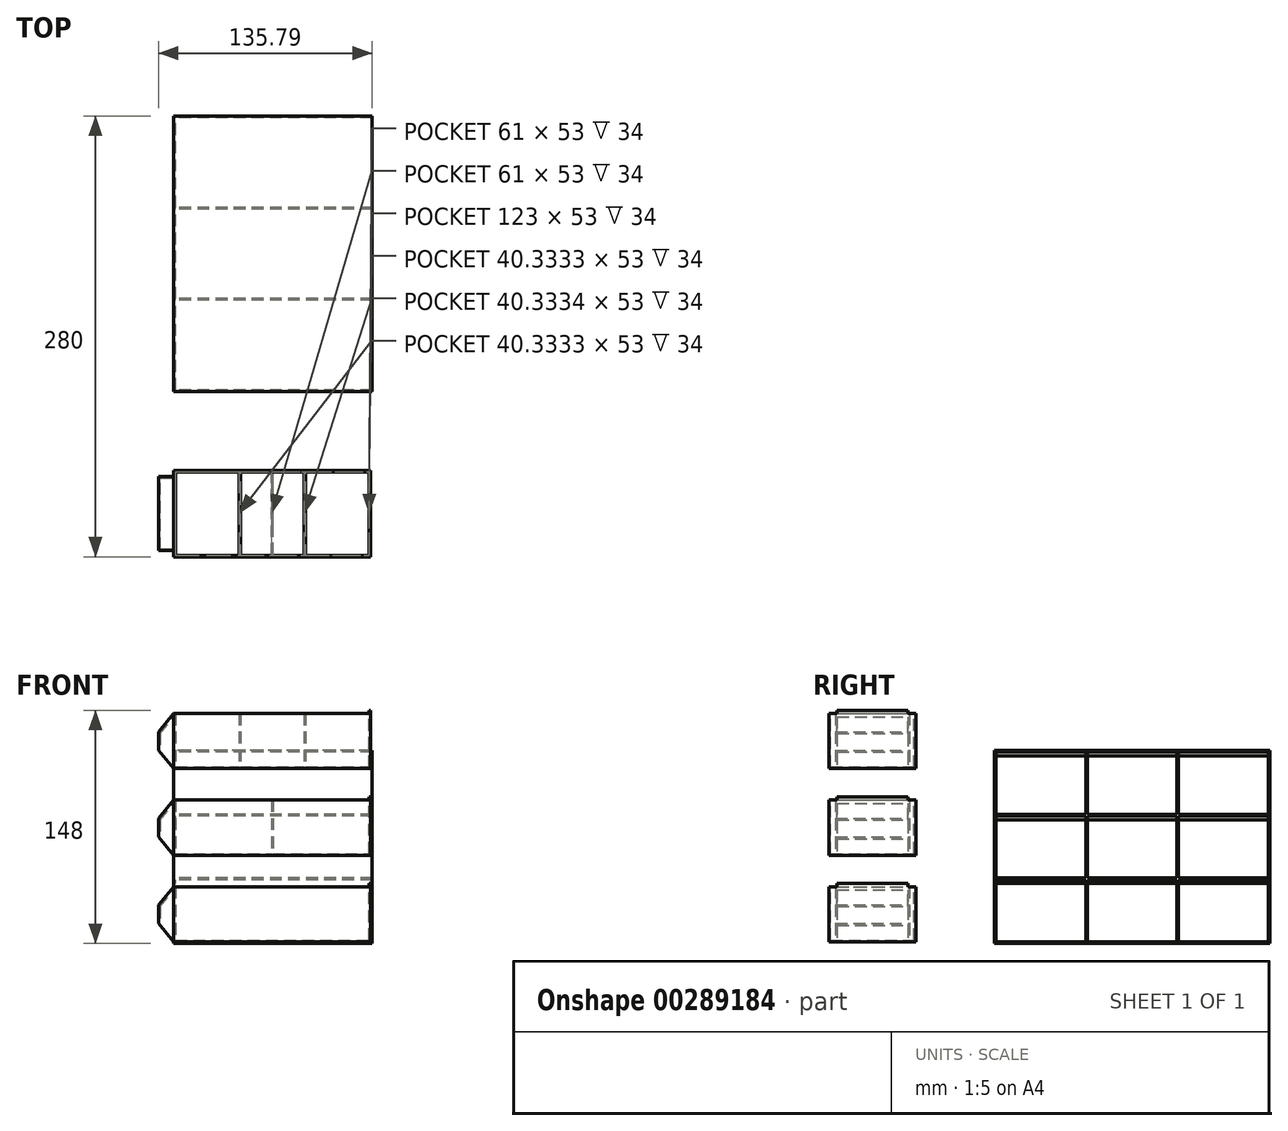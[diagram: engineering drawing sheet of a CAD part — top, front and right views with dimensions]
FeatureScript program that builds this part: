
annotation { "Feature Type Name" : "Feature", "Feature Type Description" : "" }
export const myFeature = defineFeature(function(context is Context, id is Id, definition is map)
    precondition{}
    {
        {
            assignVariable(context, id + "F0", {"name" : "DrawerDepth", "anyValue" : 125});
        }
        {
            assignVariable(context, id + "F1", {"name" : "DrawerWidth", "anyValue" : 55});
        }
        {
            assignVariable(context, id + "F2", {"name" : "Thickness", "anyValue" : 1});
        }
        {
            var Q0;
            Q0=qCreatedBy(makeId("Front.planeOp"),FACE);
            var sketch = newSketch(context, id + "F3", { "sketchPlane" : qUnion([Q0])});
            skLineSegment(sketch, "E0", {"start": v(0, 11.67) * mm, "end": v(0, 0) * mm});
            skLineSegment(sketch, "E1", {"start": v(0, 0) * mm, "end": v(125, 0) * mm});
            skLineSegment(sketch, "E2", {"start": v(125, 37) * mm, "end": v(124, 37) * mm});
            skLineSegment(sketch, "E3", {"start": v(124, 37) * mm, "end": v(124, 35) * mm});
            skLineSegment(sketch, "E4", {"start": v(0, 35) * mm, "end": v(-9.79, 23.33) * mm});
            skLineSegment(sketch, "E5", {"start": v(-9.79, 23.33) * mm, "end": v(-9.79, 11.67) * mm});
            skLineSegment(sketch, "E6", {"start": v(-9.79, 11.67) * mm, "end": v(0, 0) * mm});
            skLineSegment(sketch, "E7", {"start": v(0, 35) * mm, "end": v(0, 23.33) * mm});
            skLineSegment(sketch, "E8", {"start": v(0, 23.33) * mm, "end": v(0, 11.67) * mm});
            skLineSegment(sketch, "E9", {"start": v(0, 35) * mm, "end": v(1, 35) * mm});
            skLineSegment(sketch, "E10", {"start": v(1, 35) * mm, "end": v(124, 35) * mm});
            skLineSegment(sketch, "E11", {"start": v(125, 37) * mm, "end": v(125, 1) * mm});
            skLineSegment(sketch, "E12", {"start": v(125, 1) * mm, "end": v(125, 0) * mm});
            skLineSegment(sketch, "E13", {"start": v(1, 35) * mm, "end": v(1, 1) * mm});
            skLineSegment(sketch, "E14", {"start": v(1, 1) * mm, "end": v(124, 1) * mm});
            skLineSegment(sketch, "E15", {"start": v(124, 1) * mm, "end": v(124, 35) * mm});
            skLineSegment(sketch, "E16", {"start": v(124, 35) * mm, "end": v(125, 35) * mm});
            skLineSegment(sketch, "E17", {"start": v(-8.79, 22.5) * mm, "end": v(-8.79, 10.47) * mm});
            skLineSegment(sketch, "E18", {"start": v(-8.79, 22.5) * mm, "end": v(0, 32.97) * mm});
            skLineSegment(sketch, "E19", {"start": v(-9.79, 23.33) * mm, "end": v(-8.79, 22.5) * mm, "construction": true});
            skLineSegment(sketch, "E20", {"start": v(0, 66.67) * mm, "end": v(0, 55) * mm});
            skLineSegment(sketch, "E21", {"start": v(0, 55) * mm, "end": v(125, 55) * mm});
            skLineSegment(sketch, "E22", {"start": v(125, 92) * mm, "end": v(124, 92) * mm});
            skLineSegment(sketch, "E23", {"start": v(124, 92) * mm, "end": v(124, 90) * mm});
            skLineSegment(sketch, "E24", {"start": v(0, 90) * mm, "end": v(-9.79, 78.33) * mm});
            skLineSegment(sketch, "E25", {"start": v(-9.79, 78.33) * mm, "end": v(-9.79, 66.67) * mm});
            skLineSegment(sketch, "E26", {"start": v(-9.79, 66.67) * mm, "end": v(0, 55) * mm});
            skLineSegment(sketch, "E27", {"start": v(0, 90) * mm, "end": v(0, 78.33) * mm});
            skLineSegment(sketch, "E28", {"start": v(0, 78.33) * mm, "end": v(0, 66.67) * mm});
            skLineSegment(sketch, "E29", {"start": v(0, 90) * mm, "end": v(1, 90) * mm});
            skLineSegment(sketch, "E30", {"start": v(125, 92) * mm, "end": v(125, 56) * mm});
            skLineSegment(sketch, "E31", {"start": v(125, 56) * mm, "end": v(125, 55) * mm});
            skLineSegment(sketch, "E32", {"start": v(1, 90) * mm, "end": v(1, 56) * mm});
            skLineSegment(sketch, "E33", {"start": v(1, 56) * mm, "end": v(124, 56) * mm});
            skLineSegment(sketch, "E34", {"start": v(124, 56) * mm, "end": v(124, 90) * mm});
            skLineSegment(sketch, "E35", {"start": v(124, 90) * mm, "end": v(125, 90) * mm});
            skLineSegment(sketch, "E36", {"start": v(-8.79, 77.5) * mm, "end": v(-8.79, 65.47) * mm});
            skLineSegment(sketch, "E37", {"start": v(-8.79, 77.5) * mm, "end": v(0, 87.97) * mm});
            skLineSegment(sketch, "E38", {"start": v(-9.79, 78.33) * mm, "end": v(-8.79, 77.5) * mm, "construction": true});
            skLineSegment(sketch, "E39", {"start": v(1, 90) * mm, "end": v(62, 90) * mm});
            skLineSegment(sketch, "E40", {"start": v(62, 90) * mm, "end": v(63, 90) * mm});
            skLineSegment(sketch, "E41", {"start": v(63, 90) * mm, "end": v(124, 90) * mm});
            skLineSegment(sketch, "E42", {"start": v(62, 90) * mm, "end": v(62, 56) * mm});
            skLineSegment(sketch, "E43", {"start": v(63, 90) * mm, "end": v(63, 56) * mm});
            skLineSegment(sketch, "E44", {"start": v(0, 121.67) * mm, "end": v(0, 110) * mm});
            skLineSegment(sketch, "E45", {"start": v(0, 110) * mm, "end": v(125, 110) * mm});
            skLineSegment(sketch, "E46", {"start": v(125, 147) * mm, "end": v(124, 147) * mm});
            skLineSegment(sketch, "E47", {"start": v(124, 147) * mm, "end": v(124, 145) * mm});
            skLineSegment(sketch, "E48", {"start": v(0, 145) * mm, "end": v(-9.79, 133.33) * mm});
            skLineSegment(sketch, "E49", {"start": v(-9.79, 133.33) * mm, "end": v(-9.79, 121.67) * mm});
            skLineSegment(sketch, "E50", {"start": v(-9.79, 121.67) * mm, "end": v(0, 110) * mm});
            skLineSegment(sketch, "E51", {"start": v(0, 145) * mm, "end": v(0, 133.33) * mm});
            skLineSegment(sketch, "E52", {"start": v(0, 133.33) * mm, "end": v(0, 121.67) * mm});
            skLineSegment(sketch, "E53", {"start": v(0, 145) * mm, "end": v(1, 145) * mm});
            skLineSegment(sketch, "E54", {"start": v(125, 147) * mm, "end": v(125, 111) * mm});
            skLineSegment(sketch, "E55", {"start": v(125, 111) * mm, "end": v(125, 110) * mm});
            skLineSegment(sketch, "E56", {"start": v(1, 145) * mm, "end": v(1, 111) * mm});
            skLineSegment(sketch, "E57", {"start": v(1, 111) * mm, "end": v(124, 111) * mm});
            skLineSegment(sketch, "E58", {"start": v(124, 111) * mm, "end": v(124, 145) * mm});
            skLineSegment(sketch, "E59", {"start": v(124, 145) * mm, "end": v(125, 145) * mm});
            skLineSegment(sketch, "E60", {"start": v(-8.79, 132.5) * mm, "end": v(-8.79, 120.47) * mm});
            skLineSegment(sketch, "E61", {"start": v(-8.79, 132.5) * mm, "end": v(0, 142.97) * mm});
            skLineSegment(sketch, "E62", {"start": v(-9.79, 133.33) * mm, "end": v(-8.79, 132.5) * mm, "construction": true});
            skLineSegment(sketch, "E63", {"start": v(1, 145) * mm, "end": v(41.33, 145) * mm});
            skLineSegment(sketch, "E64", {"start": v(41.33, 145) * mm, "end": v(42.33, 145) * mm});
            skLineSegment(sketch, "E65", {"start": v(42.33, 145) * mm, "end": v(82.67, 145) * mm});
            skLineSegment(sketch, "E66", {"start": v(82.67, 145) * mm, "end": v(83.67, 145) * mm});
            skLineSegment(sketch, "E67", {"start": v(83.67, 145) * mm, "end": v(124, 145) * mm});
            skLineSegment(sketch, "E68", {"start": v(41.33, 145) * mm, "end": v(41.33, 111) * mm});
            skLineSegment(sketch, "E69", {"start": v(42.33, 145) * mm, "end": v(42.33, 111) * mm});
            skLineSegment(sketch, "E70", {"start": v(82.67, 145) * mm, "end": v(82.67, 111) * mm});
            skLineSegment(sketch, "E71", {"start": v(83.67, 145) * mm, "end": v(83.67, 111) * mm});
            skSolve(sketch);
        }
        {
            var Q0;
            Q0=makeQuery(id+"F3.imprint","IMPRINT",FACE,{"disambiguationData":[TD([[makeQuery(id+"F3.imprint","IMPRINT",EDGE,{"derivedFrom":sQuery(id+"F3.wireOp",EDGE,"E0")}),1.0]])]});
            var Q1;
            Q1=makeQuery(id+"F3.imprint","IMPRINT",FACE,{"disambiguationData":[TD([[makeQuery(id+"F3.imprint","IMPRINT",EDGE,{"derivedFrom":sQuery(id+"F3.wireOp",EDGE,"E20")}),1.0]])]});
            var Q2;
            Q2=makeQuery(id+"F3.imprint","IMPRINT",FACE,{"disambiguationData":[TD([[makeQuery(id+"F3.imprint","IMPRINT",EDGE,{"derivedFrom":sQuery(id+"F3.wireOp",EDGE,"E44")}),1.0]])]});
            var Q3;
            Q3=makeQuery(id+"F3.imprint","IMPRINT",FACE,{"disambiguationData":[TD([[makeQuery(id+"F3.imprint","IMPRINT",EDGE,{"derivedFrom":sQuery(id+"F3.wireOp",EDGE,"E40")}),-1.0]])]});
            var Q4;
            Q4=makeQuery(id+"F3.imprint","IMPRINT",FACE,{"disambiguationData":[TD([[makeQuery(id+"F3.imprint","IMPRINT",EDGE,{"derivedFrom":sQuery(id+"F3.wireOp",EDGE,"E64")}),-1.0]])]});
            var Q5;
            Q5=makeQuery(id+"F3.imprint","IMPRINT",FACE,{"disambiguationData":[TD([[makeQuery(id+"F3.imprint","IMPRINT",EDGE,{"derivedFrom":sQuery(id+"F3.wireOp",EDGE,"E66")}),-1.0]])]});
            extrude(context, id + "F4", {"entities" : qUnion([Q0, Q1, Q2, Q3, Q4, Q5]), "depth" : (getVariable(context, 'DrawerWidth')) * mm});
        }
        {
            var Q0;
            Q0=makeQuery(id+"F3.imprint","IMPRINT",FACE,{"disambiguationData":[TD([[makeQuery(id+"F3.imprint","IMPRINT",EDGE,{"derivedFrom":sQuery(id+"F3.wireOp",EDGE,"E10")}),-1.0]])]});
            var Q1;
            {var subQ0=sQuery(id+"F3.wireOp",EDGE,"E56");Q1=makeQuery(id+"F3.imprint","IMPRINT",FACE,{"disambiguationData":[TD([[makeQuery(id+"F3.imprint","IMPRINT",EDGE,{"derivedFrom":subQ0}),1.0]])]});}
            var Q2;
            Q2=makeQuery(id+"F3.imprint","IMPRINT",FACE,{"disambiguationData":[TD([[makeQuery(id+"F3.imprint","IMPRINT",EDGE,{"derivedFrom":sQuery(id+"F3.wireOp",EDGE,"E65")}),-1.0]])]});
            var Q3;
            {var subQ0=sQuery(id+"F3.wireOp",EDGE,"E58");Q3=makeQuery(id+"F3.imprint","IMPRINT",FACE,{"disambiguationData":[TD([[makeQuery(id+"F3.imprint","IMPRINT",EDGE,{"derivedFrom":subQ0}),1.0]])]});}
            var Q4;
            {var subQ0=sQuery(id+"F3.wireOp",EDGE,"E34");Q4=makeQuery(id+"F3.imprint","IMPRINT",FACE,{"disambiguationData":[TD([[makeQuery(id+"F3.imprint","IMPRINT",EDGE,{"derivedFrom":subQ0}),1.0]])]});}
            var Q5;
            {var subQ0=sQuery(id+"F3.wireOp",EDGE,"E32");Q5=makeQuery(id+"F3.imprint","IMPRINT",FACE,{"disambiguationData":[TD([[makeQuery(id+"F3.imprint","IMPRINT",EDGE,{"derivedFrom":subQ0}),1.0]])]});}
            extrude(context, id + "F5", {"entities" : qUnion([Q0, Q1, Q2, Q3, Q4, Q5]), "operationType" : NewBodyOperationType.ADD, "depth" : (getVariable(context, 'Thickness')) * mm});
        }
        {
            var Q0;
            Q0=makeQuery(id+"F3.imprint","IMPRINT",FACE,{"disambiguationData":[TD([[makeQuery(id+"F3.imprint","IMPRINT",EDGE,{"derivedFrom":sQuery(id+"F3.wireOp",EDGE,"E10")}),-1.0]])]});
            var Q1;
            {var subQ0=sQuery(id+"F3.wireOp",EDGE,"E32");Q1=makeQuery(id+"F3.imprint","IMPRINT",FACE,{"disambiguationData":[TD([[makeQuery(id+"F3.imprint","IMPRINT",EDGE,{"derivedFrom":subQ0}),1.0]])]});}
            var Q2;
            {var subQ0=sQuery(id+"F3.wireOp",EDGE,"E34");Q2=makeQuery(id+"F3.imprint","IMPRINT",FACE,{"disambiguationData":[TD([[makeQuery(id+"F3.imprint","IMPRINT",EDGE,{"derivedFrom":subQ0}),1.0]])]});}
            var Q3;
            {var subQ0=sQuery(id+"F3.wireOp",EDGE,"E56");Q3=makeQuery(id+"F3.imprint","IMPRINT",FACE,{"disambiguationData":[TD([[makeQuery(id+"F3.imprint","IMPRINT",EDGE,{"derivedFrom":subQ0}),1.0]])]});}
            var Q4;
            Q4=makeQuery(id+"F3.imprint","IMPRINT",FACE,{"disambiguationData":[TD([[makeQuery(id+"F3.imprint","IMPRINT",EDGE,{"derivedFrom":sQuery(id+"F3.wireOp",EDGE,"E65")}),-1.0]])]});
            var Q5;
            {var subQ0=sQuery(id+"F3.wireOp",EDGE,"E58");Q5=makeQuery(id+"F3.imprint","IMPRINT",FACE,{"disambiguationData":[TD([[makeQuery(id+"F3.imprint","IMPRINT",EDGE,{"derivedFrom":subQ0}),1.0]])]});}
            extrude(context, id + "F6", {"entities" : qUnion([Q0, Q1, Q2, Q3, Q4, Q5]), "operationType" : NewBodyOperationType.ADD, "depth" : (getVariable(context, 'DrawerWidth')) * mm, "hasSecondDirection" : true, "secondDirectionOppositeDirection" : false, "secondDirectionDepth" : (getVariable(context, 'DrawerWidth') - getVariable(context, 'Thickness')) * mm});
        }
        {
            var Q0;
            {var subQ0=sQuery(id+"F3.wireOp",EDGE,"E2");Q0=makeQuery(id+"F3.imprint","IMPRINT",FACE,{"disambiguationData":[TD([[makeQuery(id+"F3.imprint","IMPRINT",EDGE,{"derivedFrom":subQ0}),1.0]])]});}
            var Q1;
            {var subQ0=sQuery(id+"F3.wireOp",EDGE,"E22");Q1=makeQuery(id+"F3.imprint","IMPRINT",FACE,{"disambiguationData":[TD([[makeQuery(id+"F3.imprint","IMPRINT",EDGE,{"derivedFrom":subQ0}),1.0]])]});}
            var Q2;
            {var subQ0=sQuery(id+"F3.wireOp",EDGE,"E46");Q2=makeQuery(id+"F3.imprint","IMPRINT",FACE,{"disambiguationData":[TD([[makeQuery(id+"F3.imprint","IMPRINT",EDGE,{"derivedFrom":subQ0}),1.0]])]});}
            extrude(context, id + "F7", {"entities" : qUnion([Q0, Q1, Q2]), "operationType" : NewBodyOperationType.ADD, "depth" : (getVariable(context, 'DrawerWidth') - (5 * getVariable(context, 'Thickness'))) * mm, "hasSecondDirection" : true, "secondDirectionOppositeDirection" : false, "secondDirectionDepth" : (5 * getVariable(context, 'Thickness')) * mm});
        }
        {
            var Q0;
            {var subQ1=sQuery(id+"F3.wireOp",EDGE,"E4");Q0=makeQuery(id+"F3.imprint","IMPRINT",FACE,{"disambiguationData":[TD([[makeQuery(id+"F3.imprint","IMPRINT",EDGE,{"derivedFrom":subQ1}),1.0]])]});}
            var Q1;
            {var subQ1=sQuery(id+"F3.wireOp",EDGE,"E24");Q1=makeQuery(id+"F3.imprint","IMPRINT",FACE,{"disambiguationData":[TD([[makeQuery(id+"F3.imprint","IMPRINT",EDGE,{"derivedFrom":subQ1}),1.0]])]});}
            var Q2;
            {var subQ1=sQuery(id+"F3.wireOp",EDGE,"E48");Q2=makeQuery(id+"F3.imprint","IMPRINT",FACE,{"disambiguationData":[TD([[makeQuery(id+"F3.imprint","IMPRINT",EDGE,{"derivedFrom":subQ1}),1.0]])]});}
            extrude(context, id + "F8", {"entities" : qUnion([Q0, Q1, Q2]), "operationType" : NewBodyOperationType.ADD, "depth" : (getVariable(context, 'DrawerWidth') - (5 * getVariable(context, 'Thickness'))) * mm, "hasSecondDirection" : true, "secondDirectionOppositeDirection" : false, "secondDirectionDepth" : (5 * getVariable(context, 'Thickness')) * mm});
        }
        {
            var Q0;
            {var subQ4=sQuery(id+"F3.wireOp",EDGE,"E0");Q0=makeQuery(id+"F3.imprint","IMPRINT",FACE,{"disambiguationData":[TD([[makeQuery(id+"F3.imprint","IMPRINT",EDGE,{"derivedFrom":subQ4}),-1.0]])]});}
            var Q1;
            {var subQ1=sQuery(id+"F3.wireOp",EDGE,"E4");Q1=makeQuery(id+"F3.imprint","IMPRINT",FACE,{"disambiguationData":[TD([[makeQuery(id+"F3.imprint","IMPRINT",EDGE,{"derivedFrom":subQ1}),1.0]])]});}
            var Q2;
            {var subQ4=sQuery(id+"F3.wireOp",EDGE,"E20");Q2=makeQuery(id+"F3.imprint","IMPRINT",FACE,{"disambiguationData":[TD([[makeQuery(id+"F3.imprint","IMPRINT",EDGE,{"derivedFrom":subQ4}),-1.0]])]});}
            var Q3;
            {var subQ1=sQuery(id+"F3.wireOp",EDGE,"E24");Q3=makeQuery(id+"F3.imprint","IMPRINT",FACE,{"disambiguationData":[TD([[makeQuery(id+"F3.imprint","IMPRINT",EDGE,{"derivedFrom":subQ1}),1.0]])]});}
            var Q4;
            {var subQ1=sQuery(id+"F3.wireOp",EDGE,"E48");Q4=makeQuery(id+"F3.imprint","IMPRINT",FACE,{"disambiguationData":[TD([[makeQuery(id+"F3.imprint","IMPRINT",EDGE,{"derivedFrom":subQ1}),1.0]])]});}
            var Q5;
            {var subQ4=sQuery(id+"F3.wireOp",EDGE,"E44");Q5=makeQuery(id+"F3.imprint","IMPRINT",FACE,{"disambiguationData":[TD([[makeQuery(id+"F3.imprint","IMPRINT",EDGE,{"derivedFrom":subQ4}),-1.0]])]});}
            extrude(context, id + "F9", {"entities" : qUnion([Q0, Q1, Q2, Q3, Q4, Q5]), "operationType" : NewBodyOperationType.ADD, "depth" : (getVariable(context, 'DrawerWidth') - (4 * getVariable(context, 'Thickness'))) * mm, "hasSecondDirection" : true, "secondDirectionOppositeDirection" : false, "secondDirectionDepth" : (getVariable(context, 'DrawerWidth') - (5 * getVariable(context, 'Thickness'))) * mm});
        }
        {
            var Q0;
            {var subQ4=sQuery(id+"F3.wireOp",EDGE,"E0");Q0=makeQuery(id+"F3.imprint","IMPRINT",FACE,{"disambiguationData":[TD([[makeQuery(id+"F3.imprint","IMPRINT",EDGE,{"derivedFrom":subQ4}),-1.0]])]});}
            var Q1;
            {var subQ1=sQuery(id+"F3.wireOp",EDGE,"E4");Q1=makeQuery(id+"F3.imprint","IMPRINT",FACE,{"disambiguationData":[TD([[makeQuery(id+"F3.imprint","IMPRINT",EDGE,{"derivedFrom":subQ1}),1.0]])]});}
            var Q2;
            {var subQ1=sQuery(id+"F3.wireOp",EDGE,"E24");Q2=makeQuery(id+"F3.imprint","IMPRINT",FACE,{"disambiguationData":[TD([[makeQuery(id+"F3.imprint","IMPRINT",EDGE,{"derivedFrom":subQ1}),1.0]])]});}
            var Q3;
            {var subQ4=sQuery(id+"F3.wireOp",EDGE,"E20");Q3=makeQuery(id+"F3.imprint","IMPRINT",FACE,{"disambiguationData":[TD([[makeQuery(id+"F3.imprint","IMPRINT",EDGE,{"derivedFrom":subQ4}),-1.0]])]});}
            var Q4;
            {var subQ1=sQuery(id+"F3.wireOp",EDGE,"E48");Q4=makeQuery(id+"F3.imprint","IMPRINT",FACE,{"disambiguationData":[TD([[makeQuery(id+"F3.imprint","IMPRINT",EDGE,{"derivedFrom":subQ1}),1.0]])]});}
            var Q5;
            {var subQ4=sQuery(id+"F3.wireOp",EDGE,"E44");Q5=makeQuery(id+"F3.imprint","IMPRINT",FACE,{"disambiguationData":[TD([[makeQuery(id+"F3.imprint","IMPRINT",EDGE,{"derivedFrom":subQ4}),-1.0]])]});}
            extrude(context, id + "F10", {"entities" : qUnion([Q0, Q1, Q2, Q3, Q4, Q5]), "operationType" : NewBodyOperationType.ADD, "depth" : (5 * getVariable(context, 'Thickness')) * mm, "hasSecondDirection" : true, "secondDirectionOppositeDirection" : false, "secondDirectionDepth" : (4 * getVariable(context, 'Thickness')) * mm});
        }
        {
            var Q0;
            Q0=qCreatedBy(makeId("Right.planeOp"),FACE);
            var sketch = newSketch(context, id + "F11", { "sketchPlane" : qUnion([Q0])});
            skLineSegment(sketch, "E72", {"start": v(50, -1) * mm, "end": v(50, 0) * mm});
            skLineSegment(sketch, "E73", {"start": v(50, 0) * mm, "end": v(50, 37) * mm});
            skLineSegment(sketch, "E74", {"start": v(50, 37) * mm, "end": v(50, 39.5) * mm});
            skLineSegment(sketch, "E75", {"start": v(50, 39.5) * mm, "end": v(50, 40.5) * mm});
            skLineSegment(sketch, "E76", {"start": v(50, 40.5) * mm, "end": v(50, 77.5) * mm});
            skLineSegment(sketch, "E77", {"start": v(50, 77.5) * mm, "end": v(50, 80) * mm});
            skLineSegment(sketch, "E78", {"start": v(50, 80) * mm, "end": v(50, 81) * mm});
            skLineSegment(sketch, "E79", {"start": v(50, 81) * mm, "end": v(50, 118) * mm});
            skLineSegment(sketch, "E80", {"start": v(50, 118) * mm, "end": v(50, 120.5) * mm});
            skLineSegment(sketch, "E81", {"start": v(50, -1) * mm, "end": v(51, -1) * mm});
            skLineSegment(sketch, "E82", {"start": v(51, -1) * mm, "end": v(108, -1) * mm});
            skLineSegment(sketch, "E83", {"start": v(108, -1) * mm, "end": v(109, -1) * mm});
            skLineSegment(sketch, "E84", {"start": v(109, -1) * mm, "end": v(166, -1) * mm});
            skLineSegment(sketch, "E85", {"start": v(166, -1) * mm, "end": v(167, -1) * mm});
            skLineSegment(sketch, "E86", {"start": v(167, -1) * mm, "end": v(224, -1) * mm});
            skLineSegment(sketch, "E87", {"start": v(50, 120.5) * mm, "end": v(50, 121.5) * mm});
            skLineSegment(sketch, "E88", {"start": v(225, -1) * mm, "end": v(224, -1) * mm});
            skLineSegment(sketch, "E89", {"start": v(51, 0) * mm, "end": v(51, 39.5) * mm});
            skLineSegment(sketch, "E90", {"start": v(108, 0) * mm, "end": v(108, 39.5) * mm});
            skLineSegment(sketch, "E91", {"start": v(109, 0) * mm, "end": v(109, 39.5) * mm});
            skLineSegment(sketch, "E92", {"start": v(166, 0) * mm, "end": v(166, 39.5) * mm});
            skLineSegment(sketch, "E93", {"start": v(167, 0) * mm, "end": v(167, 39.5) * mm});
            skLineSegment(sketch, "E94", {"start": v(224, 0) * mm, "end": v(224, 39.5) * mm});
            skLineSegment(sketch, "E95", {"start": v(51, 120.5) * mm, "end": v(108, 120.5) * mm});
            skLineSegment(sketch, "E96", {"start": v(51, 118) * mm, "end": v(108, 118) * mm});
            skLineSegment(sketch, "E97", {"start": v(51, 81) * mm, "end": v(108, 81) * mm});
            skLineSegment(sketch, "E98", {"start": v(51, 80) * mm, "end": v(108, 80) * mm});
            skLineSegment(sketch, "E99", {"start": v(51, 77.5) * mm, "end": v(108, 77.5) * mm});
            skLineSegment(sketch, "E100", {"start": v(51, 40.5) * mm, "end": v(108, 40.5) * mm});
            skLineSegment(sketch, "E101", {"start": v(51, 39.5) * mm, "end": v(108, 39.5) * mm});
            skLineSegment(sketch, "E102", {"start": v(51, 37) * mm, "end": v(108, 37) * mm});
            skLineSegment(sketch, "E103", {"start": v(51, 0) * mm, "end": v(108, 0) * mm});
            skLineSegment(sketch, "E104.trimOffspring", {"start": v(109, 0) * mm, "end": v(166, 0) * mm});
            skLineSegment(sketch, "E105.trimOffspring", {"start": v(51, 40.5) * mm, "end": v(51, 80) * mm});
            skLineSegment(sketch, "E106.trimOffspring", {"start": v(108, 40.5) * mm, "end": v(108, 80) * mm});
            skLineSegment(sketch, "E107.trimOffspring", {"start": v(109, 39.5) * mm, "end": v(166, 39.5) * mm});
            skLineSegment(sketch, "E108.trimOffspring", {"start": v(109, 40.5) * mm, "end": v(166, 40.5) * mm});
            skLineSegment(sketch, "E109.trimOffspring", {"start": v(109, 37) * mm, "end": v(166, 37) * mm});
            skLineSegment(sketch, "E110.trimOffspring", {"start": v(109, 40.5) * mm, "end": v(109, 80) * mm});
            skLineSegment(sketch, "E111.trimOffspring", {"start": v(166, 40.5) * mm, "end": v(166, 80) * mm});
            skLineSegment(sketch, "E112.trimOffspring", {"start": v(167, 40.5) * mm, "end": v(224, 40.5) * mm});
            skLineSegment(sketch, "E113.trimOffspring", {"start": v(167, 40.5) * mm, "end": v(167, 80) * mm});
            skLineSegment(sketch, "E114.trimOffspring", {"start": v(167, 39.5) * mm, "end": v(224, 39.5) * mm});
            skLineSegment(sketch, "E115.trimOffspring", {"start": v(167, 37) * mm, "end": v(224, 37) * mm});
            skLineSegment(sketch, "E116.trimOffspring", {"start": v(167, 0) * mm, "end": v(224, 0) * mm});
            skLineSegment(sketch, "E117.trimOffspring", {"start": v(224, 40.5) * mm, "end": v(224, 80) * mm});
            skLineSegment(sketch, "E118.trimOffspring", {"start": v(224, 81) * mm, "end": v(224, 120.5) * mm});
            skLineSegment(sketch, "E119.trimOffspring", {"start": v(167, 120.5) * mm, "end": v(224, 120.5) * mm});
            skLineSegment(sketch, "E120.trimOffspring", {"start": v(167, 118) * mm, "end": v(224, 118) * mm});
            skLineSegment(sketch, "E121.trimOffspring", {"start": v(167, 81) * mm, "end": v(224, 81) * mm});
            skLineSegment(sketch, "E122.trimOffspring", {"start": v(167, 80) * mm, "end": v(224, 80) * mm});
            skLineSegment(sketch, "E123.trimOffspring", {"start": v(167, 77.5) * mm, "end": v(224, 77.5) * mm});
            skLineSegment(sketch, "E124.trimOffspring", {"start": v(167, 81) * mm, "end": v(167, 120.5) * mm});
            skLineSegment(sketch, "E125.trimOffspring", {"start": v(166, 81) * mm, "end": v(166, 120.5) * mm});
            skLineSegment(sketch, "E126.trimOffspring", {"start": v(109, 120.5) * mm, "end": v(166, 120.5) * mm});
            skLineSegment(sketch, "E127.trimOffspring", {"start": v(109, 118) * mm, "end": v(166, 118) * mm});
            skLineSegment(sketch, "E128.trimOffspring", {"start": v(109, 81) * mm, "end": v(166, 81) * mm});
            skLineSegment(sketch, "E129.trimOffspring", {"start": v(108, 81) * mm, "end": v(108, 120.5) * mm});
            skLineSegment(sketch, "E130.trimOffspring", {"start": v(109, 81) * mm, "end": v(109, 120.5) * mm});
            skLineSegment(sketch, "E131.trimOffspring", {"start": v(109, 80) * mm, "end": v(166, 80) * mm});
            skLineSegment(sketch, "E132.trimOffspring", {"start": v(109, 77.5) * mm, "end": v(166, 77.5) * mm});
            skLineSegment(sketch, "E133.trimOffspring", {"start": v(51, 81) * mm, "end": v(51, 120.5) * mm});
            skLineSegment(sketch, "E134", {"start": v(50, 121.5) * mm, "end": v(50, 158.5) * mm});
            skLineSegment(sketch, "E135", {"start": v(50, 158.5) * mm, "end": v(50, 161) * mm});
            skLineSegment(sketch, "E136", {"start": v(50, 161) * mm, "end": v(50, 162) * mm});
            skLineSegment(sketch, "E137", {"start": v(50, 162) * mm, "end": v(50, 199) * mm});
            skLineSegment(sketch, "E138", {"start": v(50, 199) * mm, "end": v(50, 201.5) * mm});
            skLineSegment(sketch, "E139", {"start": v(50, 201.5) * mm, "end": v(50, 202.5) * mm});
            skLineSegment(sketch, "E140", {"start": v(50, 202.5) * mm, "end": v(50, 239.5) * mm});
            skLineSegment(sketch, "E141", {"start": v(50, 239.5) * mm, "end": v(50, 242) * mm});
            skLineSegment(sketch, "E142", {"start": v(50, 242) * mm, "end": v(50, 243) * mm});
            skLineSegment(sketch, "E143", {"start": v(51, 121.5) * mm, "end": v(51, 161) * mm});
            skLineSegment(sketch, "E144", {"start": v(108, 121.5) * mm, "end": v(108, 161) * mm});
            skLineSegment(sketch, "E145", {"start": v(109, 121.5) * mm, "end": v(109, 161) * mm});
            skLineSegment(sketch, "E146", {"start": v(166, 121.5) * mm, "end": v(166, 161) * mm});
            skLineSegment(sketch, "E147", {"start": v(167, 121.5) * mm, "end": v(167, 161) * mm});
            skLineSegment(sketch, "E148", {"start": v(224, 121.5) * mm, "end": v(224, 161) * mm});
            skLineSegment(sketch, "E149", {"start": v(51, 242) * mm, "end": v(108, 242) * mm});
            skLineSegment(sketch, "E150", {"start": v(51, 239.5) * mm, "end": v(108, 239.5) * mm});
            skLineSegment(sketch, "E151", {"start": v(51, 202.5) * mm, "end": v(108, 202.5) * mm});
            skLineSegment(sketch, "E152", {"start": v(51, 201.5) * mm, "end": v(108, 201.5) * mm});
            skLineSegment(sketch, "E153", {"start": v(51, 199) * mm, "end": v(108, 199) * mm});
            skLineSegment(sketch, "E154", {"start": v(51, 162) * mm, "end": v(108, 162) * mm});
            skLineSegment(sketch, "E155", {"start": v(51, 161) * mm, "end": v(108, 161) * mm});
            skLineSegment(sketch, "E156", {"start": v(51, 158.5) * mm, "end": v(108, 158.5) * mm});
            skLineSegment(sketch, "E157", {"start": v(51, 121.5) * mm, "end": v(108, 121.5) * mm});
            skLineSegment(sketch, "E158.trimOffspring", {"start": v(109, 121.5) * mm, "end": v(166, 121.5) * mm});
            skLineSegment(sketch, "E159.trimOffspring", {"start": v(51, 162) * mm, "end": v(51, 201.5) * mm});
            skLineSegment(sketch, "E160.trimOffspring", {"start": v(108, 162) * mm, "end": v(108, 201.5) * mm});
            skLineSegment(sketch, "E161.trimOffspring", {"start": v(109, 161) * mm, "end": v(166, 161) * mm});
            skLineSegment(sketch, "E162.trimOffspring", {"start": v(109, 162) * mm, "end": v(166, 162) * mm});
            skLineSegment(sketch, "E163.trimOffspring", {"start": v(109, 158.5) * mm, "end": v(166, 158.5) * mm});
            skLineSegment(sketch, "E164.trimOffspring", {"start": v(109, 162) * mm, "end": v(109, 201.5) * mm});
            skLineSegment(sketch, "E165.trimOffspring", {"start": v(166, 162) * mm, "end": v(166, 201.5) * mm});
            skLineSegment(sketch, "E166.trimOffspring", {"start": v(167, 162) * mm, "end": v(224, 162) * mm});
            skLineSegment(sketch, "E167.trimOffspring", {"start": v(167, 162) * mm, "end": v(167, 201.5) * mm});
            skLineSegment(sketch, "E168.trimOffspring", {"start": v(167, 161) * mm, "end": v(224, 161) * mm});
            skLineSegment(sketch, "E169.trimOffspring", {"start": v(167, 158.5) * mm, "end": v(224, 158.5) * mm});
            skLineSegment(sketch, "E170.trimOffspring", {"start": v(167, 121.5) * mm, "end": v(224, 121.5) * mm});
            skLineSegment(sketch, "E171.trimOffspring", {"start": v(224, 162) * mm, "end": v(224, 201.5) * mm});
            skLineSegment(sketch, "E172.trimOffspring", {"start": v(224, 202.5) * mm, "end": v(224, 242) * mm});
            skLineSegment(sketch, "E173.trimOffspring", {"start": v(167, 242) * mm, "end": v(224, 242) * mm});
            skLineSegment(sketch, "E174.trimOffspring", {"start": v(167, 239.5) * mm, "end": v(224, 239.5) * mm});
            skLineSegment(sketch, "E175.trimOffspring", {"start": v(167, 202.5) * mm, "end": v(224, 202.5) * mm});
            skLineSegment(sketch, "E176.trimOffspring", {"start": v(167, 201.5) * mm, "end": v(224, 201.5) * mm});
            skLineSegment(sketch, "E177.trimOffspring", {"start": v(167, 199) * mm, "end": v(224, 199) * mm});
            skLineSegment(sketch, "E178.trimOffspring", {"start": v(167, 202.5) * mm, "end": v(167, 242) * mm});
            skLineSegment(sketch, "E179.trimOffspring", {"start": v(166, 202.5) * mm, "end": v(166, 242) * mm});
            skLineSegment(sketch, "E180.trimOffspring", {"start": v(109, 242) * mm, "end": v(166, 242) * mm});
            skLineSegment(sketch, "E181.trimOffspring", {"start": v(109, 239.5) * mm, "end": v(166, 239.5) * mm});
            skLineSegment(sketch, "E182.trimOffspring", {"start": v(109, 202.5) * mm, "end": v(166, 202.5) * mm});
            skLineSegment(sketch, "E183.trimOffspring", {"start": v(108, 202.5) * mm, "end": v(108, 242) * mm});
            skLineSegment(sketch, "E184.trimOffspring", {"start": v(109, 202.5) * mm, "end": v(109, 242) * mm});
            skLineSegment(sketch, "E185.trimOffspring", {"start": v(109, 201.5) * mm, "end": v(166, 201.5) * mm});
            skLineSegment(sketch, "E186.trimOffspring", {"start": v(109, 199) * mm, "end": v(166, 199) * mm});
            skLineSegment(sketch, "E187.trimOffspring", {"start": v(51, 202.5) * mm, "end": v(51, 242) * mm});
            skLineSegment(sketch, "E188", {"start": v(50, 243) * mm, "end": v(50, 280) * mm});
            skLineSegment(sketch, "E189", {"start": v(50, 280) * mm, "end": v(50, 282.5) * mm});
            skLineSegment(sketch, "E190", {"start": v(50, 282.5) * mm, "end": v(50, 283.5) * mm});
            skLineSegment(sketch, "E191", {"start": v(50, 283.5) * mm, "end": v(50, 320.5) * mm});
            skLineSegment(sketch, "E192", {"start": v(50, 320.5) * mm, "end": v(50, 323) * mm});
            skLineSegment(sketch, "E193", {"start": v(50, 323) * mm, "end": v(50, 324) * mm});
            skLineSegment(sketch, "E194", {"start": v(50, 324) * mm, "end": v(50, 361) * mm});
            skLineSegment(sketch, "E195", {"start": v(50, 361) * mm, "end": v(50, 363.5) * mm});
            skLineSegment(sketch, "E196", {"start": v(51, 243) * mm, "end": v(51, 282.5) * mm});
            skLineSegment(sketch, "E197", {"start": v(108, 243) * mm, "end": v(108, 282.5) * mm});
            skLineSegment(sketch, "E198", {"start": v(109, 243) * mm, "end": v(109, 282.5) * mm});
            skLineSegment(sketch, "E199", {"start": v(166, 243) * mm, "end": v(166, 282.5) * mm});
            skLineSegment(sketch, "E200", {"start": v(167, 243) * mm, "end": v(167, 282.5) * mm});
            skLineSegment(sketch, "E201", {"start": v(224, 243) * mm, "end": v(224, 282.5) * mm});
            skLineSegment(sketch, "E202", {"start": v(51, 363.5) * mm, "end": v(108, 363.5) * mm});
            skLineSegment(sketch, "E203", {"start": v(51, 361) * mm, "end": v(108, 361) * mm});
            skLineSegment(sketch, "E204", {"start": v(51, 324) * mm, "end": v(108, 324) * mm});
            skLineSegment(sketch, "E205", {"start": v(51, 323) * mm, "end": v(108, 323) * mm});
            skLineSegment(sketch, "E206", {"start": v(51, 320.5) * mm, "end": v(108, 320.5) * mm});
            skLineSegment(sketch, "E207", {"start": v(51, 283.5) * mm, "end": v(108, 283.5) * mm});
            skLineSegment(sketch, "E208", {"start": v(51, 282.5) * mm, "end": v(108, 282.5) * mm});
            skLineSegment(sketch, "E209", {"start": v(51, 280) * mm, "end": v(108, 280) * mm});
            skLineSegment(sketch, "E210", {"start": v(51, 243) * mm, "end": v(108, 243) * mm});
            skLineSegment(sketch, "E211.trimOffspring", {"start": v(109, 243) * mm, "end": v(166, 243) * mm});
            skLineSegment(sketch, "E212.trimOffspring", {"start": v(51, 283.5) * mm, "end": v(51, 323) * mm});
            skLineSegment(sketch, "E213.trimOffspring", {"start": v(108, 283.5) * mm, "end": v(108, 323) * mm});
            skLineSegment(sketch, "E214.trimOffspring", {"start": v(109, 282.5) * mm, "end": v(166, 282.5) * mm});
            skLineSegment(sketch, "E215.trimOffspring", {"start": v(109, 283.5) * mm, "end": v(166, 283.5) * mm});
            skLineSegment(sketch, "E216.trimOffspring", {"start": v(109, 280) * mm, "end": v(166, 280) * mm});
            skLineSegment(sketch, "E217.trimOffspring", {"start": v(109, 283.5) * mm, "end": v(109, 323) * mm});
            skLineSegment(sketch, "E218.trimOffspring", {"start": v(166, 283.5) * mm, "end": v(166, 323) * mm});
            skLineSegment(sketch, "E219.trimOffspring", {"start": v(167, 283.5) * mm, "end": v(224, 283.5) * mm});
            skLineSegment(sketch, "E220.trimOffspring", {"start": v(167, 283.5) * mm, "end": v(167, 323) * mm});
            skLineSegment(sketch, "E221.trimOffspring", {"start": v(167, 282.5) * mm, "end": v(224, 282.5) * mm});
            skLineSegment(sketch, "E222.trimOffspring", {"start": v(167, 280) * mm, "end": v(224, 280) * mm});
            skLineSegment(sketch, "E223.trimOffspring", {"start": v(167, 243) * mm, "end": v(224, 243) * mm});
            skLineSegment(sketch, "E224.trimOffspring", {"start": v(224, 283.5) * mm, "end": v(224, 323) * mm});
            skLineSegment(sketch, "E225.trimOffspring", {"start": v(224, 324) * mm, "end": v(224, 363.5) * mm});
            skLineSegment(sketch, "E226.trimOffspring", {"start": v(167, 363.5) * mm, "end": v(224, 363.5) * mm});
            skLineSegment(sketch, "E227.trimOffspring", {"start": v(167, 361) * mm, "end": v(224, 361) * mm});
            skLineSegment(sketch, "E228.trimOffspring", {"start": v(167, 324) * mm, "end": v(224, 324) * mm});
            skLineSegment(sketch, "E229.trimOffspring", {"start": v(167, 323) * mm, "end": v(224, 323) * mm});
            skLineSegment(sketch, "E230.trimOffspring", {"start": v(167, 320.5) * mm, "end": v(224, 320.5) * mm});
            skLineSegment(sketch, "E231.trimOffspring", {"start": v(167, 324) * mm, "end": v(167, 363.5) * mm});
            skLineSegment(sketch, "E232.trimOffspring", {"start": v(166, 324) * mm, "end": v(166, 363.5) * mm});
            skLineSegment(sketch, "E233.trimOffspring", {"start": v(109, 363.5) * mm, "end": v(166, 363.5) * mm});
            skLineSegment(sketch, "E234.trimOffspring", {"start": v(109, 361) * mm, "end": v(166, 361) * mm});
            skLineSegment(sketch, "E235.trimOffspring", {"start": v(109, 324) * mm, "end": v(166, 324) * mm});
            skLineSegment(sketch, "E236.trimOffspring", {"start": v(108, 324) * mm, "end": v(108, 363.5) * mm});
            skLineSegment(sketch, "E237.trimOffspring", {"start": v(109, 324) * mm, "end": v(109, 363.5) * mm});
            skLineSegment(sketch, "E238.trimOffspring", {"start": v(109, 323) * mm, "end": v(166, 323) * mm});
            skLineSegment(sketch, "E239.trimOffspring", {"start": v(109, 320.5) * mm, "end": v(166, 320.5) * mm});
            skLineSegment(sketch, "E240.trimOffspring", {"start": v(51, 324) * mm, "end": v(51, 363.5) * mm});
            skLineSegment(sketch, "E241", {"start": v(50, 363.5) * mm, "end": v(50, 364.5) * mm});
            skLineSegment(sketch, "E242", {"start": v(50, 364.5) * mm, "end": v(50, 401.5) * mm});
            skLineSegment(sketch, "E243", {"start": v(50, 401.5) * mm, "end": v(50, 404) * mm});
            skLineSegment(sketch, "E244", {"start": v(51, 404) * mm, "end": v(108, 404) * mm});
            skLineSegment(sketch, "E245", {"start": v(51, 401.5) * mm, "end": v(108, 401.5) * mm});
            skLineSegment(sketch, "E246", {"start": v(51, 364.5) * mm, "end": v(108, 364.5) * mm});
            skLineSegment(sketch, "E247.trimOffspring", {"start": v(224, 364.5) * mm, "end": v(224, 404) * mm});
            skLineSegment(sketch, "E248.trimOffspring", {"start": v(167, 404) * mm, "end": v(224, 404) * mm});
            skLineSegment(sketch, "E249.trimOffspring", {"start": v(167, 401.5) * mm, "end": v(224, 401.5) * mm});
            skLineSegment(sketch, "E250.trimOffspring", {"start": v(167, 364.5) * mm, "end": v(224, 364.5) * mm});
            skLineSegment(sketch, "E251.trimOffspring", {"start": v(167, 364.5) * mm, "end": v(167, 404) * mm});
            skLineSegment(sketch, "E252.trimOffspring", {"start": v(166, 364.5) * mm, "end": v(166, 404) * mm});
            skLineSegment(sketch, "E253.trimOffspring", {"start": v(109, 404) * mm, "end": v(166, 404) * mm});
            skLineSegment(sketch, "E254.trimOffspring", {"start": v(109, 401.5) * mm, "end": v(166, 401.5) * mm});
            skLineSegment(sketch, "E255.trimOffspring", {"start": v(109, 364.5) * mm, "end": v(166, 364.5) * mm});
            skLineSegment(sketch, "E256.trimOffspring", {"start": v(108, 364.5) * mm, "end": v(108, 404) * mm});
            skLineSegment(sketch, "E257.trimOffspring", {"start": v(109, 364.5) * mm, "end": v(109, 404) * mm});
            skLineSegment(sketch, "E258.trimOffspring", {"start": v(51, 364.5) * mm, "end": v(51, 404) * mm});
            skLineSegment(sketch, "E259", {"start": v(225, -1) * mm, "end": v(282, -1) * mm});
            skLineSegment(sketch, "E260", {"start": v(282, -1) * mm, "end": v(283, -1) * mm});
            skLineSegment(sketch, "E261", {"start": v(283, -1) * mm, "end": v(340, -1) * mm});
            skLineSegment(sketch, "E262", {"start": v(340, -1) * mm, "end": v(341, -1) * mm});
            skLineSegment(sketch, "E263", {"start": v(341, -1) * mm, "end": v(398, -1) * mm});
            skLineSegment(sketch, "E264", {"start": v(399, -1) * mm, "end": v(398, -1) * mm});
            skLineSegment(sketch, "E265", {"start": v(225, 0) * mm, "end": v(225, 39.5) * mm});
            skLineSegment(sketch, "E266", {"start": v(282, 0) * mm, "end": v(282, 39.5) * mm});
            skLineSegment(sketch, "E267", {"start": v(283, 0) * mm, "end": v(283, 39.5) * mm});
            skLineSegment(sketch, "E268", {"start": v(340, 0) * mm, "end": v(340, 39.5) * mm});
            skLineSegment(sketch, "E269", {"start": v(341, 0) * mm, "end": v(341, 39.5) * mm});
            skLineSegment(sketch, "E270", {"start": v(398, 0) * mm, "end": v(398, 39.5) * mm});
            skLineSegment(sketch, "E271", {"start": v(225, 120.5) * mm, "end": v(282, 120.5) * mm});
            skLineSegment(sketch, "E272", {"start": v(225, 118) * mm, "end": v(282, 118) * mm});
            skLineSegment(sketch, "E273", {"start": v(225, 81) * mm, "end": v(282, 81) * mm});
            skLineSegment(sketch, "E274", {"start": v(225, 80) * mm, "end": v(282, 80) * mm});
            skLineSegment(sketch, "E275", {"start": v(225, 77.5) * mm, "end": v(282, 77.5) * mm});
            skLineSegment(sketch, "E276", {"start": v(225, 40.5) * mm, "end": v(282, 40.5) * mm});
            skLineSegment(sketch, "E277", {"start": v(225, 39.5) * mm, "end": v(282, 39.5) * mm});
            skLineSegment(sketch, "E278", {"start": v(225, 37) * mm, "end": v(282, 37) * mm});
            skLineSegment(sketch, "E279", {"start": v(225, 0) * mm, "end": v(282, 0) * mm});
            skLineSegment(sketch, "E280.trimOffspring", {"start": v(283, 0) * mm, "end": v(340, 0) * mm});
            skLineSegment(sketch, "E281.trimOffspring", {"start": v(225, 40.5) * mm, "end": v(225, 80) * mm});
            skLineSegment(sketch, "E282.trimOffspring", {"start": v(282, 40.5) * mm, "end": v(282, 80) * mm});
            skLineSegment(sketch, "E283.trimOffspring", {"start": v(283, 39.5) * mm, "end": v(340, 39.5) * mm});
            skLineSegment(sketch, "E284.trimOffspring", {"start": v(283, 40.5) * mm, "end": v(340, 40.5) * mm});
            skLineSegment(sketch, "E285.trimOffspring", {"start": v(283, 37) * mm, "end": v(340, 37) * mm});
            skLineSegment(sketch, "E286.trimOffspring", {"start": v(283, 40.5) * mm, "end": v(283, 80) * mm});
            skLineSegment(sketch, "E287.trimOffspring", {"start": v(340, 40.5) * mm, "end": v(340, 80) * mm});
            skLineSegment(sketch, "E288.trimOffspring", {"start": v(341, 40.5) * mm, "end": v(398, 40.5) * mm});
            skLineSegment(sketch, "E289.trimOffspring", {"start": v(341, 40.5) * mm, "end": v(341, 80) * mm});
            skLineSegment(sketch, "E290.trimOffspring", {"start": v(341, 39.5) * mm, "end": v(398, 39.5) * mm});
            skLineSegment(sketch, "E291.trimOffspring", {"start": v(341, 37) * mm, "end": v(398, 37) * mm});
            skLineSegment(sketch, "E292.trimOffspring", {"start": v(341, 0) * mm, "end": v(398, 0) * mm});
            skLineSegment(sketch, "E293.trimOffspring", {"start": v(398, 40.5) * mm, "end": v(398, 80) * mm});
            skLineSegment(sketch, "E294.trimOffspring", {"start": v(398, 81) * mm, "end": v(398, 120.5) * mm});
            skLineSegment(sketch, "E295.trimOffspring", {"start": v(341, 120.5) * mm, "end": v(398, 120.5) * mm});
            skLineSegment(sketch, "E296.trimOffspring", {"start": v(341, 118) * mm, "end": v(398, 118) * mm});
            skLineSegment(sketch, "E297.trimOffspring", {"start": v(341, 81) * mm, "end": v(398, 81) * mm});
            skLineSegment(sketch, "E298.trimOffspring", {"start": v(341, 80) * mm, "end": v(398, 80) * mm});
            skLineSegment(sketch, "E299.trimOffspring", {"start": v(341, 77.5) * mm, "end": v(398, 77.5) * mm});
            skLineSegment(sketch, "E300.trimOffspring", {"start": v(341, 81) * mm, "end": v(341, 120.5) * mm});
            skLineSegment(sketch, "E301.trimOffspring", {"start": v(340, 81) * mm, "end": v(340, 120.5) * mm});
            skLineSegment(sketch, "E302.trimOffspring", {"start": v(283, 120.5) * mm, "end": v(340, 120.5) * mm});
            skLineSegment(sketch, "E303.trimOffspring", {"start": v(283, 118) * mm, "end": v(340, 118) * mm});
            skLineSegment(sketch, "E304.trimOffspring", {"start": v(283, 81) * mm, "end": v(340, 81) * mm});
            skLineSegment(sketch, "E305.trimOffspring", {"start": v(282, 81) * mm, "end": v(282, 120.5) * mm});
            skLineSegment(sketch, "E306.trimOffspring", {"start": v(283, 81) * mm, "end": v(283, 120.5) * mm});
            skLineSegment(sketch, "E307.trimOffspring", {"start": v(283, 80) * mm, "end": v(340, 80) * mm});
            skLineSegment(sketch, "E308.trimOffspring", {"start": v(283, 77.5) * mm, "end": v(340, 77.5) * mm});
            skLineSegment(sketch, "E309.trimOffspring", {"start": v(225, 81) * mm, "end": v(225, 120.5) * mm});
            skLineSegment(sketch, "E310", {"start": v(225, 121.5) * mm, "end": v(225, 161) * mm});
            skLineSegment(sketch, "E311", {"start": v(282, 121.5) * mm, "end": v(282, 161) * mm});
            skLineSegment(sketch, "E312", {"start": v(283, 121.5) * mm, "end": v(283, 161) * mm});
            skLineSegment(sketch, "E313", {"start": v(340, 121.5) * mm, "end": v(340, 161) * mm});
            skLineSegment(sketch, "E314", {"start": v(341, 121.5) * mm, "end": v(341, 161) * mm});
            skLineSegment(sketch, "E315", {"start": v(398, 121.5) * mm, "end": v(398, 161) * mm});
            skLineSegment(sketch, "E316", {"start": v(225, 242) * mm, "end": v(282, 242) * mm});
            skLineSegment(sketch, "E317", {"start": v(225, 202.5) * mm, "end": v(282, 202.5) * mm});
            skLineSegment(sketch, "E318", {"start": v(225, 201.5) * mm, "end": v(282, 201.5) * mm});
            skLineSegment(sketch, "E319", {"start": v(225, 199) * mm, "end": v(282, 199) * mm});
            skLineSegment(sketch, "E320", {"start": v(225, 162) * mm, "end": v(282, 162) * mm});
            skLineSegment(sketch, "E321", {"start": v(225, 161) * mm, "end": v(282, 161) * mm});
            skLineSegment(sketch, "E322", {"start": v(225, 158.5) * mm, "end": v(282, 158.5) * mm});
            skLineSegment(sketch, "E323", {"start": v(225, 121.5) * mm, "end": v(282, 121.5) * mm});
            skLineSegment(sketch, "E324.trimOffspring", {"start": v(283, 121.5) * mm, "end": v(340, 121.5) * mm});
            skLineSegment(sketch, "E325.trimOffspring", {"start": v(225, 162) * mm, "end": v(225, 201.5) * mm});
            skLineSegment(sketch, "E326.trimOffspring", {"start": v(282, 162) * mm, "end": v(282, 201.5) * mm});
            skLineSegment(sketch, "E327.trimOffspring", {"start": v(283, 161) * mm, "end": v(340, 161) * mm});
            skLineSegment(sketch, "E328.trimOffspring", {"start": v(283, 162) * mm, "end": v(340, 162) * mm});
            skLineSegment(sketch, "E329.trimOffspring", {"start": v(283, 158.5) * mm, "end": v(340, 158.5) * mm});
            skLineSegment(sketch, "E330.trimOffspring", {"start": v(283, 162) * mm, "end": v(283, 201.5) * mm});
            skLineSegment(sketch, "E331.trimOffspring", {"start": v(340, 162) * mm, "end": v(340, 201.5) * mm});
            skLineSegment(sketch, "E332.trimOffspring", {"start": v(341, 162) * mm, "end": v(398, 162) * mm});
            skLineSegment(sketch, "E333.trimOffspring", {"start": v(341, 162) * mm, "end": v(341, 201.5) * mm});
            skLineSegment(sketch, "E334.trimOffspring", {"start": v(341, 161) * mm, "end": v(398, 161) * mm});
            skLineSegment(sketch, "E335.trimOffspring", {"start": v(341, 158.5) * mm, "end": v(398, 158.5) * mm});
            skLineSegment(sketch, "E336.trimOffspring", {"start": v(341, 121.5) * mm, "end": v(398, 121.5) * mm});
            skLineSegment(sketch, "E337.trimOffspring", {"start": v(398, 162) * mm, "end": v(398, 201.5) * mm});
            skLineSegment(sketch, "E338.trimOffspring", {"start": v(398, 202.5) * mm, "end": v(398, 242) * mm});
            skLineSegment(sketch, "E339.trimOffspring", {"start": v(341, 242) * mm, "end": v(398, 242) * mm});
            skLineSegment(sketch, "E340.trimOffspring", {"start": v(341, 202.5) * mm, "end": v(398, 202.5) * mm});
            skLineSegment(sketch, "E341.trimOffspring", {"start": v(341, 201.5) * mm, "end": v(398, 201.5) * mm});
            skLineSegment(sketch, "E342.trimOffspring", {"start": v(341, 199) * mm, "end": v(398, 199) * mm});
            skLineSegment(sketch, "E343.trimOffspring", {"start": v(341, 202.5) * mm, "end": v(341, 242) * mm});
            skLineSegment(sketch, "E344.trimOffspring", {"start": v(340, 202.5) * mm, "end": v(340, 242) * mm});
            skLineSegment(sketch, "E345.trimOffspring", {"start": v(283, 242) * mm, "end": v(340, 242) * mm});
            skLineSegment(sketch, "E346.trimOffspring", {"start": v(283, 202.5) * mm, "end": v(340, 202.5) * mm});
            skLineSegment(sketch, "E347.trimOffspring", {"start": v(282, 202.5) * mm, "end": v(282, 242) * mm});
            skLineSegment(sketch, "E348.trimOffspring", {"start": v(283, 202.5) * mm, "end": v(283, 242) * mm});
            skLineSegment(sketch, "E349.trimOffspring", {"start": v(283, 201.5) * mm, "end": v(340, 201.5) * mm});
            skLineSegment(sketch, "E350.trimOffspring", {"start": v(283, 199) * mm, "end": v(340, 199) * mm});
            skLineSegment(sketch, "E351.trimOffspring", {"start": v(225, 202.5) * mm, "end": v(225, 242) * mm});
            skLineSegment(sketch, "E352", {"start": v(225, 243) * mm, "end": v(225, 282.5) * mm});
            skLineSegment(sketch, "E353", {"start": v(282, 243) * mm, "end": v(282, 282.5) * mm});
            skLineSegment(sketch, "E354", {"start": v(283, 243) * mm, "end": v(283, 282.5) * mm});
            skLineSegment(sketch, "E355", {"start": v(340, 243) * mm, "end": v(340, 282.5) * mm});
            skLineSegment(sketch, "E356", {"start": v(341, 243) * mm, "end": v(341, 282.5) * mm});
            skLineSegment(sketch, "E357", {"start": v(398, 243) * mm, "end": v(398, 282.5) * mm});
            skLineSegment(sketch, "E358", {"start": v(225, 363.5) * mm, "end": v(282, 363.5) * mm});
            skLineSegment(sketch, "E359", {"start": v(225, 361) * mm, "end": v(282, 361) * mm});
            skLineSegment(sketch, "E360", {"start": v(225, 324) * mm, "end": v(282, 324) * mm});
            skLineSegment(sketch, "E361", {"start": v(225, 323) * mm, "end": v(282, 323) * mm});
            skLineSegment(sketch, "E362", {"start": v(225, 320.5) * mm, "end": v(282, 320.5) * mm});
            skLineSegment(sketch, "E363", {"start": v(225, 283.5) * mm, "end": v(282, 283.5) * mm});
            skLineSegment(sketch, "E364", {"start": v(225, 282.5) * mm, "end": v(282, 282.5) * mm});
            skLineSegment(sketch, "E365", {"start": v(225, 280) * mm, "end": v(282, 280) * mm});
            skLineSegment(sketch, "E366", {"start": v(225, 243) * mm, "end": v(282, 243) * mm});
            skLineSegment(sketch, "E367.trimOffspring", {"start": v(283, 243) * mm, "end": v(340, 243) * mm});
            skLineSegment(sketch, "E368.trimOffspring", {"start": v(225, 283.5) * mm, "end": v(225, 323) * mm});
            skLineSegment(sketch, "E369.trimOffspring", {"start": v(282, 283.5) * mm, "end": v(282, 323) * mm});
            skLineSegment(sketch, "E370.trimOffspring", {"start": v(283, 282.5) * mm, "end": v(340, 282.5) * mm});
            skLineSegment(sketch, "E371.trimOffspring", {"start": v(283, 283.5) * mm, "end": v(340, 283.5) * mm});
            skLineSegment(sketch, "E372.trimOffspring", {"start": v(283, 280) * mm, "end": v(340, 280) * mm});
            skLineSegment(sketch, "E373.trimOffspring", {"start": v(283, 283.5) * mm, "end": v(283, 323) * mm});
            skLineSegment(sketch, "E374.trimOffspring", {"start": v(340, 283.5) * mm, "end": v(340, 323) * mm});
            skLineSegment(sketch, "E375.trimOffspring", {"start": v(341, 283.5) * mm, "end": v(398, 283.5) * mm});
            skLineSegment(sketch, "E376.trimOffspring", {"start": v(341, 283.5) * mm, "end": v(341, 323) * mm});
            skLineSegment(sketch, "E377.trimOffspring", {"start": v(341, 282.5) * mm, "end": v(398, 282.5) * mm});
            skLineSegment(sketch, "E378.trimOffspring", {"start": v(341, 280) * mm, "end": v(398, 280) * mm});
            skLineSegment(sketch, "E379.trimOffspring", {"start": v(341, 243) * mm, "end": v(398, 243) * mm});
            skLineSegment(sketch, "E380.trimOffspring", {"start": v(398, 283.5) * mm, "end": v(398, 323) * mm});
            skLineSegment(sketch, "E381.trimOffspring", {"start": v(398, 324) * mm, "end": v(398, 363.5) * mm});
            skLineSegment(sketch, "E382.trimOffspring", {"start": v(341, 363.5) * mm, "end": v(398, 363.5) * mm});
            skLineSegment(sketch, "E383.trimOffspring", {"start": v(341, 361) * mm, "end": v(398, 361) * mm});
            skLineSegment(sketch, "E384.trimOffspring", {"start": v(341, 324) * mm, "end": v(398, 324) * mm});
            skLineSegment(sketch, "E385.trimOffspring", {"start": v(341, 323) * mm, "end": v(398, 323) * mm});
            skLineSegment(sketch, "E386.trimOffspring", {"start": v(341, 320.5) * mm, "end": v(398, 320.5) * mm});
            skLineSegment(sketch, "E387.trimOffspring", {"start": v(341, 324) * mm, "end": v(341, 363.5) * mm});
            skLineSegment(sketch, "E388.trimOffspring", {"start": v(340, 324) * mm, "end": v(340, 363.5) * mm});
            skLineSegment(sketch, "E389.trimOffspring", {"start": v(283, 363.5) * mm, "end": v(340, 363.5) * mm});
            skLineSegment(sketch, "E390.trimOffspring", {"start": v(283, 361) * mm, "end": v(340, 361) * mm});
            skLineSegment(sketch, "E391.trimOffspring", {"start": v(283, 324) * mm, "end": v(340, 324) * mm});
            skLineSegment(sketch, "E392.trimOffspring", {"start": v(282, 324) * mm, "end": v(282, 363.5) * mm});
            skLineSegment(sketch, "E393.trimOffspring", {"start": v(283, 324) * mm, "end": v(283, 363.5) * mm});
            skLineSegment(sketch, "E394.trimOffspring", {"start": v(283, 323) * mm, "end": v(340, 323) * mm});
            skLineSegment(sketch, "E395.trimOffspring", {"start": v(283, 320.5) * mm, "end": v(340, 320.5) * mm});
            skLineSegment(sketch, "E396.trimOffspring", {"start": v(225, 324) * mm, "end": v(225, 363.5) * mm});
            skLineSegment(sketch, "E397", {"start": v(225, 404) * mm, "end": v(282, 404) * mm});
            skLineSegment(sketch, "E398", {"start": v(225, 401.5) * mm, "end": v(282, 401.5) * mm});
            skLineSegment(sketch, "E399", {"start": v(225, 364.5) * mm, "end": v(282, 364.5) * mm});
            skLineSegment(sketch, "E400.trimOffspring", {"start": v(398, 364.5) * mm, "end": v(398, 404) * mm});
            skLineSegment(sketch, "E401.trimOffspring", {"start": v(341, 404) * mm, "end": v(398, 404) * mm});
            skLineSegment(sketch, "E402.trimOffspring", {"start": v(341, 401.5) * mm, "end": v(398, 401.5) * mm});
            skLineSegment(sketch, "E403.trimOffspring", {"start": v(341, 364.5) * mm, "end": v(398, 364.5) * mm});
            skLineSegment(sketch, "E404.trimOffspring", {"start": v(341, 364.5) * mm, "end": v(341, 404) * mm});
            skLineSegment(sketch, "E405.trimOffspring", {"start": v(340, 364.5) * mm, "end": v(340, 404) * mm});
            skLineSegment(sketch, "E406.trimOffspring", {"start": v(283, 404) * mm, "end": v(340, 404) * mm});
            skLineSegment(sketch, "E407.trimOffspring", {"start": v(283, 401.5) * mm, "end": v(340, 401.5) * mm});
            skLineSegment(sketch, "E408.trimOffspring", {"start": v(283, 364.5) * mm, "end": v(340, 364.5) * mm});
            skLineSegment(sketch, "E409.trimOffspring", {"start": v(282, 364.5) * mm, "end": v(282, 404) * mm});
            skLineSegment(sketch, "E410.trimOffspring", {"start": v(283, 364.5) * mm, "end": v(283, 404) * mm});
            skLineSegment(sketch, "E411.trimOffspring", {"start": v(225, 364.5) * mm, "end": v(225, 404) * mm});
            skLineSegment(sketch, "E412", {"start": v(225, 239.5) * mm, "end": v(282, 239.5) * mm});
            skLineSegment(sketch, "E413.trimOffspring", {"start": v(341, 239.5) * mm, "end": v(398, 239.5) * mm});
            skLineSegment(sketch, "E414.trimOffspring", {"start": v(283, 239.5) * mm, "end": v(340, 239.5) * mm});
            skLineSegment(sketch, "E415", {"start": v(399, -1) * mm, "end": v(456, -1) * mm});
            skLineSegment(sketch, "E416", {"start": v(457, -1) * mm, "end": v(456, -1) * mm});
            skLineSegment(sketch, "E417", {"start": v(399, 0) * mm, "end": v(399, 39.5) * mm});
            skLineSegment(sketch, "E418", {"start": v(456, 0) * mm, "end": v(456, 39.5) * mm});
            skLineSegment(sketch, "E419.trimOffspring", {"start": v(399, 40.5) * mm, "end": v(456, 40.5) * mm});
            skLineSegment(sketch, "E420.trimOffspring", {"start": v(399, 40.5) * mm, "end": v(399, 80) * mm});
            skLineSegment(sketch, "E421.trimOffspring", {"start": v(399, 39.5) * mm, "end": v(456, 39.5) * mm});
            skLineSegment(sketch, "E422.trimOffspring", {"start": v(399, 37) * mm, "end": v(456, 37) * mm});
            skLineSegment(sketch, "E423.trimOffspring", {"start": v(399, 0) * mm, "end": v(456, 0) * mm});
            skLineSegment(sketch, "E424.trimOffspring", {"start": v(456, 40.5) * mm, "end": v(456, 80) * mm});
            skLineSegment(sketch, "E425.trimOffspring", {"start": v(456, 81) * mm, "end": v(456, 120.5) * mm});
            skLineSegment(sketch, "E426.trimOffspring", {"start": v(399, 120.5) * mm, "end": v(456, 120.5) * mm});
            skLineSegment(sketch, "E427.trimOffspring", {"start": v(399, 118) * mm, "end": v(456, 118) * mm});
            skLineSegment(sketch, "E428.trimOffspring", {"start": v(399, 81) * mm, "end": v(456, 81) * mm});
            skLineSegment(sketch, "E429.trimOffspring", {"start": v(399, 80) * mm, "end": v(456, 80) * mm});
            skLineSegment(sketch, "E430.trimOffspring", {"start": v(399, 77.5) * mm, "end": v(456, 77.5) * mm});
            skLineSegment(sketch, "E431.trimOffspring", {"start": v(399, 81) * mm, "end": v(399, 120.5) * mm});
            skLineSegment(sketch, "E432", {"start": v(399, 121.5) * mm, "end": v(399, 161) * mm});
            skLineSegment(sketch, "E433", {"start": v(456, 121.5) * mm, "end": v(456, 161) * mm});
            skLineSegment(sketch, "E434.trimOffspring", {"start": v(399, 162) * mm, "end": v(456, 162) * mm});
            skLineSegment(sketch, "E435.trimOffspring", {"start": v(399, 162) * mm, "end": v(399, 201.5) * mm});
            skLineSegment(sketch, "E436.trimOffspring", {"start": v(399, 161) * mm, "end": v(456, 161) * mm});
            skLineSegment(sketch, "E437.trimOffspring", {"start": v(399, 158.5) * mm, "end": v(456, 158.5) * mm});
            skLineSegment(sketch, "E438.trimOffspring", {"start": v(399, 121.5) * mm, "end": v(456, 121.5) * mm});
            skLineSegment(sketch, "E439.trimOffspring", {"start": v(456, 162) * mm, "end": v(456, 201.5) * mm});
            skLineSegment(sketch, "E440.trimOffspring", {"start": v(456, 202.5) * mm, "end": v(456, 242) * mm});
            skLineSegment(sketch, "E441.trimOffspring", {"start": v(399, 242) * mm, "end": v(456, 242) * mm});
            skLineSegment(sketch, "E442.trimOffspring", {"start": v(399, 239.5) * mm, "end": v(456, 239.5) * mm});
            skLineSegment(sketch, "E443.trimOffspring", {"start": v(399, 202.5) * mm, "end": v(456, 202.5) * mm});
            skLineSegment(sketch, "E444.trimOffspring", {"start": v(399, 201.5) * mm, "end": v(456, 201.5) * mm});
            skLineSegment(sketch, "E445.trimOffspring", {"start": v(399, 199) * mm, "end": v(456, 199) * mm});
            skLineSegment(sketch, "E446.trimOffspring", {"start": v(399, 202.5) * mm, "end": v(399, 242) * mm});
            skLineSegment(sketch, "E447", {"start": v(399, 243) * mm, "end": v(399, 282.5) * mm});
            skLineSegment(sketch, "E448", {"start": v(456, 243) * mm, "end": v(456, 282.5) * mm});
            skLineSegment(sketch, "E449.trimOffspring", {"start": v(399, 283.5) * mm, "end": v(456, 283.5) * mm});
            skLineSegment(sketch, "E450.trimOffspring", {"start": v(399, 283.5) * mm, "end": v(399, 323) * mm});
            skLineSegment(sketch, "E451.trimOffspring", {"start": v(399, 282.5) * mm, "end": v(456, 282.5) * mm});
            skLineSegment(sketch, "E452.trimOffspring", {"start": v(399, 280) * mm, "end": v(456, 280) * mm});
            skLineSegment(sketch, "E453.trimOffspring", {"start": v(399, 243) * mm, "end": v(456, 243) * mm});
            skLineSegment(sketch, "E454.trimOffspring", {"start": v(456, 283.5) * mm, "end": v(456, 323) * mm});
            skLineSegment(sketch, "E455.trimOffspring", {"start": v(456, 324) * mm, "end": v(456, 363.5) * mm});
            skLineSegment(sketch, "E456.trimOffspring", {"start": v(399, 363.5) * mm, "end": v(456, 363.5) * mm});
            skLineSegment(sketch, "E457.trimOffspring", {"start": v(399, 361) * mm, "end": v(456, 361) * mm});
            skLineSegment(sketch, "E458.trimOffspring", {"start": v(399, 324) * mm, "end": v(456, 324) * mm});
            skLineSegment(sketch, "E459.trimOffspring", {"start": v(399, 323) * mm, "end": v(456, 323) * mm});
            skLineSegment(sketch, "E460.trimOffspring", {"start": v(399, 320.5) * mm, "end": v(456, 320.5) * mm});
            skLineSegment(sketch, "E461.trimOffspring", {"start": v(399, 324) * mm, "end": v(399, 363.5) * mm});
            skLineSegment(sketch, "E462.trimOffspring", {"start": v(456, 364.5) * mm, "end": v(456, 404) * mm});
            skLineSegment(sketch, "E463.trimOffspring", {"start": v(399, 404) * mm, "end": v(456, 404) * mm});
            skLineSegment(sketch, "E464.trimOffspring", {"start": v(399, 401.5) * mm, "end": v(456, 401.5) * mm});
            skLineSegment(sketch, "E465.trimOffspring", {"start": v(399, 364.5) * mm, "end": v(456, 364.5) * mm});
            skLineSegment(sketch, "E466.trimOffspring", {"start": v(399, 364.5) * mm, "end": v(399, 404) * mm});
            skLineSegment(sketch, "E467", {"start": v(457, -1) * mm, "end": v(514, -1) * mm});
            skLineSegment(sketch, "E468", {"start": v(514, -1) * mm, "end": v(515, -1) * mm});
            skLineSegment(sketch, "E469", {"start": v(515, -1) * mm, "end": v(572, -1) * mm});
            skLineSegment(sketch, "E470", {"start": v(572, -1) * mm, "end": v(573, -1) * mm});
            skLineSegment(sketch, "E471", {"start": v(573, -1) * mm, "end": v(630, -1) * mm});
            skLineSegment(sketch, "E472", {"start": v(631, 405) * mm, "end": v(631, -1) * mm});
            skLineSegment(sketch, "E473", {"start": v(631, -1) * mm, "end": v(630, -1) * mm});
            skLineSegment(sketch, "E474", {"start": v(457, 0) * mm, "end": v(457, 39.5) * mm});
            skLineSegment(sketch, "E475", {"start": v(514, 0) * mm, "end": v(514, 39.5) * mm});
            skLineSegment(sketch, "E476", {"start": v(515, 0) * mm, "end": v(515, 39.5) * mm});
            skLineSegment(sketch, "E477", {"start": v(572, 0) * mm, "end": v(572, 39.5) * mm});
            skLineSegment(sketch, "E478", {"start": v(573, 0) * mm, "end": v(573, 39.5) * mm});
            skLineSegment(sketch, "E479", {"start": v(630, 0) * mm, "end": v(630, 39.5) * mm});
            skLineSegment(sketch, "E480", {"start": v(457, 120.5) * mm, "end": v(514, 120.5) * mm});
            skLineSegment(sketch, "E481", {"start": v(457, 118) * mm, "end": v(514, 118) * mm});
            skLineSegment(sketch, "E482", {"start": v(457, 81) * mm, "end": v(514, 81) * mm});
            skLineSegment(sketch, "E483", {"start": v(457, 80) * mm, "end": v(514, 80) * mm});
            skLineSegment(sketch, "E484", {"start": v(457, 77.5) * mm, "end": v(514, 77.5) * mm});
            skLineSegment(sketch, "E485", {"start": v(457, 40.5) * mm, "end": v(514, 40.5) * mm});
            skLineSegment(sketch, "E486", {"start": v(457, 39.5) * mm, "end": v(514, 39.5) * mm});
            skLineSegment(sketch, "E487", {"start": v(457, 37) * mm, "end": v(514, 37) * mm});
            skLineSegment(sketch, "E488", {"start": v(457, 0) * mm, "end": v(514, 0) * mm});
            skLineSegment(sketch, "E489.trimOffspring", {"start": v(515, 0) * mm, "end": v(572, 0) * mm});
            skLineSegment(sketch, "E490.trimOffspring", {"start": v(457, 40.5) * mm, "end": v(457, 80) * mm});
            skLineSegment(sketch, "E491.trimOffspring", {"start": v(514, 40.5) * mm, "end": v(514, 80) * mm});
            skLineSegment(sketch, "E492.trimOffspring", {"start": v(515, 39.5) * mm, "end": v(572, 39.5) * mm});
            skLineSegment(sketch, "E493.trimOffspring", {"start": v(515, 40.5) * mm, "end": v(572, 40.5) * mm});
            skLineSegment(sketch, "E494.trimOffspring", {"start": v(515, 37) * mm, "end": v(572, 37) * mm});
            skLineSegment(sketch, "E495.trimOffspring", {"start": v(515, 40.5) * mm, "end": v(515, 80) * mm});
            skLineSegment(sketch, "E496.trimOffspring", {"start": v(572, 40.5) * mm, "end": v(572, 80) * mm});
            skLineSegment(sketch, "E497.trimOffspring", {"start": v(573, 40.5) * mm, "end": v(630, 40.5) * mm});
            skLineSegment(sketch, "E498.trimOffspring", {"start": v(573, 40.5) * mm, "end": v(573, 80) * mm});
            skLineSegment(sketch, "E499.trimOffspring", {"start": v(573, 39.5) * mm, "end": v(630, 39.5) * mm});
            skLineSegment(sketch, "E500.trimOffspring", {"start": v(573, 37) * mm, "end": v(630, 37) * mm});
            skLineSegment(sketch, "E501.trimOffspring", {"start": v(573, 0) * mm, "end": v(630, 0) * mm});
            skLineSegment(sketch, "E502.trimOffspring", {"start": v(630, 40.5) * mm, "end": v(630, 80) * mm});
            skLineSegment(sketch, "E503.trimOffspring", {"start": v(630, 81) * mm, "end": v(630, 120.5) * mm});
            skLineSegment(sketch, "E504.trimOffspring", {"start": v(573, 120.5) * mm, "end": v(630, 120.5) * mm});
            skLineSegment(sketch, "E505.trimOffspring", {"start": v(573, 118) * mm, "end": v(630, 118) * mm});
            skLineSegment(sketch, "E506.trimOffspring", {"start": v(573, 81) * mm, "end": v(630, 81) * mm});
            skLineSegment(sketch, "E507.trimOffspring", {"start": v(573, 80) * mm, "end": v(630, 80) * mm});
            skLineSegment(sketch, "E508.trimOffspring", {"start": v(573, 77.5) * mm, "end": v(630, 77.5) * mm});
            skLineSegment(sketch, "E509.trimOffspring", {"start": v(573, 81) * mm, "end": v(573, 120.5) * mm});
            skLineSegment(sketch, "E510.trimOffspring", {"start": v(572, 81) * mm, "end": v(572, 120.5) * mm});
            skLineSegment(sketch, "E511.trimOffspring", {"start": v(515, 120.5) * mm, "end": v(572, 120.5) * mm});
            skLineSegment(sketch, "E512.trimOffspring", {"start": v(515, 118) * mm, "end": v(572, 118) * mm});
            skLineSegment(sketch, "E513.trimOffspring", {"start": v(515, 81) * mm, "end": v(572, 81) * mm});
            skLineSegment(sketch, "E514.trimOffspring", {"start": v(514, 81) * mm, "end": v(514, 120.5) * mm});
            skLineSegment(sketch, "E515.trimOffspring", {"start": v(515, 81) * mm, "end": v(515, 120.5) * mm});
            skLineSegment(sketch, "E516.trimOffspring", {"start": v(515, 80) * mm, "end": v(572, 80) * mm});
            skLineSegment(sketch, "E517.trimOffspring", {"start": v(515, 77.5) * mm, "end": v(572, 77.5) * mm});
            skLineSegment(sketch, "E518.trimOffspring", {"start": v(457, 81) * mm, "end": v(457, 120.5) * mm});
            skLineSegment(sketch, "E519", {"start": v(457, 121.5) * mm, "end": v(457, 161) * mm});
            skLineSegment(sketch, "E520", {"start": v(514, 121.5) * mm, "end": v(514, 161) * mm});
            skLineSegment(sketch, "E521", {"start": v(515, 121.5) * mm, "end": v(515, 161) * mm});
            skLineSegment(sketch, "E522", {"start": v(572, 121.5) * mm, "end": v(572, 161) * mm});
            skLineSegment(sketch, "E523", {"start": v(573, 121.5) * mm, "end": v(573, 161) * mm});
            skLineSegment(sketch, "E524", {"start": v(630, 121.5) * mm, "end": v(630, 161) * mm});
            skLineSegment(sketch, "E525", {"start": v(457, 242) * mm, "end": v(514, 242) * mm});
            skLineSegment(sketch, "E526", {"start": v(457, 202.5) * mm, "end": v(514, 202.5) * mm});
            skLineSegment(sketch, "E527", {"start": v(457, 201.5) * mm, "end": v(514, 201.5) * mm});
            skLineSegment(sketch, "E528", {"start": v(457, 199) * mm, "end": v(514, 199) * mm});
            skLineSegment(sketch, "E529", {"start": v(457, 162) * mm, "end": v(514, 162) * mm});
            skLineSegment(sketch, "E530", {"start": v(457, 161) * mm, "end": v(514, 161) * mm});
            skLineSegment(sketch, "E531", {"start": v(457, 158.5) * mm, "end": v(514, 158.5) * mm});
            skLineSegment(sketch, "E532", {"start": v(457, 121.5) * mm, "end": v(514, 121.5) * mm});
            skLineSegment(sketch, "E533.trimOffspring", {"start": v(515, 121.5) * mm, "end": v(572, 121.5) * mm});
            skLineSegment(sketch, "E534.trimOffspring", {"start": v(457, 162) * mm, "end": v(457, 201.5) * mm});
            skLineSegment(sketch, "E535.trimOffspring", {"start": v(514, 162) * mm, "end": v(514, 201.5) * mm});
            skLineSegment(sketch, "E536.trimOffspring", {"start": v(515, 161) * mm, "end": v(572, 161) * mm});
            skLineSegment(sketch, "E537.trimOffspring", {"start": v(515, 162) * mm, "end": v(572, 162) * mm});
            skLineSegment(sketch, "E538.trimOffspring", {"start": v(515, 158.5) * mm, "end": v(572, 158.5) * mm});
            skLineSegment(sketch, "E539.trimOffspring", {"start": v(515, 162) * mm, "end": v(515, 201.5) * mm});
            skLineSegment(sketch, "E540.trimOffspring", {"start": v(572, 162) * mm, "end": v(572, 201.5) * mm});
            skLineSegment(sketch, "E541.trimOffspring", {"start": v(573, 162) * mm, "end": v(630, 162) * mm});
            skLineSegment(sketch, "E542.trimOffspring", {"start": v(573, 162) * mm, "end": v(573, 201.5) * mm});
            skLineSegment(sketch, "E543.trimOffspring", {"start": v(573, 161) * mm, "end": v(630, 161) * mm});
            skLineSegment(sketch, "E544.trimOffspring", {"start": v(573, 158.5) * mm, "end": v(630, 158.5) * mm});
            skLineSegment(sketch, "E545.trimOffspring", {"start": v(573, 121.5) * mm, "end": v(630, 121.5) * mm});
            skLineSegment(sketch, "E546.trimOffspring", {"start": v(630, 162) * mm, "end": v(630, 201.5) * mm});
            skLineSegment(sketch, "E547.trimOffspring", {"start": v(630, 202.5) * mm, "end": v(630, 242) * mm});
            skLineSegment(sketch, "E548.trimOffspring", {"start": v(573, 242) * mm, "end": v(630, 242) * mm});
            skLineSegment(sketch, "E549.trimOffspring", {"start": v(573, 202.5) * mm, "end": v(630, 202.5) * mm});
            skLineSegment(sketch, "E550.trimOffspring", {"start": v(573, 201.5) * mm, "end": v(630, 201.5) * mm});
            skLineSegment(sketch, "E551.trimOffspring", {"start": v(573, 199) * mm, "end": v(630, 199) * mm});
            skLineSegment(sketch, "E552.trimOffspring", {"start": v(573, 202.5) * mm, "end": v(573, 242) * mm});
            skLineSegment(sketch, "E553.trimOffspring", {"start": v(572, 202.5) * mm, "end": v(572, 242) * mm});
            skLineSegment(sketch, "E554.trimOffspring", {"start": v(515, 242) * mm, "end": v(572, 242) * mm});
            skLineSegment(sketch, "E555.trimOffspring", {"start": v(515, 202.5) * mm, "end": v(572, 202.5) * mm});
            skLineSegment(sketch, "E556.trimOffspring", {"start": v(514, 202.5) * mm, "end": v(514, 242) * mm});
            skLineSegment(sketch, "E557.trimOffspring", {"start": v(515, 202.5) * mm, "end": v(515, 242) * mm});
            skLineSegment(sketch, "E558.trimOffspring", {"start": v(515, 201.5) * mm, "end": v(572, 201.5) * mm});
            skLineSegment(sketch, "E559.trimOffspring", {"start": v(515, 199) * mm, "end": v(572, 199) * mm});
            skLineSegment(sketch, "E560.trimOffspring", {"start": v(457, 202.5) * mm, "end": v(457, 242) * mm});
            skLineSegment(sketch, "E561", {"start": v(457, 243) * mm, "end": v(457, 282.5) * mm});
            skLineSegment(sketch, "E562", {"start": v(514, 243) * mm, "end": v(514, 282.5) * mm});
            skLineSegment(sketch, "E563", {"start": v(515, 243) * mm, "end": v(515, 282.5) * mm});
            skLineSegment(sketch, "E564", {"start": v(572, 243) * mm, "end": v(572, 282.5) * mm});
            skLineSegment(sketch, "E565", {"start": v(573, 243) * mm, "end": v(573, 282.5) * mm});
            skLineSegment(sketch, "E566", {"start": v(630, 243) * mm, "end": v(630, 282.5) * mm});
            skLineSegment(sketch, "E567", {"start": v(457, 363.5) * mm, "end": v(514, 363.5) * mm});
            skLineSegment(sketch, "E568", {"start": v(457, 361) * mm, "end": v(514, 361) * mm});
            skLineSegment(sketch, "E569", {"start": v(457, 324) * mm, "end": v(514, 324) * mm});
            skLineSegment(sketch, "E570", {"start": v(457, 323) * mm, "end": v(514, 323) * mm});
            skLineSegment(sketch, "E571", {"start": v(457, 320.5) * mm, "end": v(514, 320.5) * mm});
            skLineSegment(sketch, "E572", {"start": v(457, 283.5) * mm, "end": v(514, 283.5) * mm});
            skLineSegment(sketch, "E573", {"start": v(457, 282.5) * mm, "end": v(514, 282.5) * mm});
            skLineSegment(sketch, "E574", {"start": v(457, 280) * mm, "end": v(514, 280) * mm});
            skLineSegment(sketch, "E575", {"start": v(457, 243) * mm, "end": v(514, 243) * mm});
            skLineSegment(sketch, "E576.trimOffspring", {"start": v(515, 243) * mm, "end": v(572, 243) * mm});
            skLineSegment(sketch, "E577.trimOffspring", {"start": v(457, 283.5) * mm, "end": v(457, 323) * mm});
            skLineSegment(sketch, "E578.trimOffspring", {"start": v(514, 283.5) * mm, "end": v(514, 323) * mm});
            skLineSegment(sketch, "E579.trimOffspring", {"start": v(515, 282.5) * mm, "end": v(572, 282.5) * mm});
            skLineSegment(sketch, "E580.trimOffspring", {"start": v(515, 283.5) * mm, "end": v(572, 283.5) * mm});
            skLineSegment(sketch, "E581.trimOffspring", {"start": v(515, 280) * mm, "end": v(572, 280) * mm});
            skLineSegment(sketch, "E582.trimOffspring", {"start": v(515, 283.5) * mm, "end": v(515, 323) * mm});
            skLineSegment(sketch, "E583.trimOffspring", {"start": v(572, 283.5) * mm, "end": v(572, 323) * mm});
            skLineSegment(sketch, "E584.trimOffspring", {"start": v(573, 283.5) * mm, "end": v(630, 283.5) * mm});
            skLineSegment(sketch, "E585.trimOffspring", {"start": v(573, 283.5) * mm, "end": v(573, 323) * mm});
            skLineSegment(sketch, "E586.trimOffspring", {"start": v(573, 282.5) * mm, "end": v(630, 282.5) * mm});
            skLineSegment(sketch, "E587.trimOffspring", {"start": v(573, 280) * mm, "end": v(630, 280) * mm});
            skLineSegment(sketch, "E588.trimOffspring", {"start": v(573, 243) * mm, "end": v(630, 243) * mm});
            skLineSegment(sketch, "E589.trimOffspring", {"start": v(630, 283.5) * mm, "end": v(630, 323) * mm});
            skLineSegment(sketch, "E590.trimOffspring", {"start": v(630, 324) * mm, "end": v(630, 363.5) * mm});
            skLineSegment(sketch, "E591.trimOffspring", {"start": v(573, 363.5) * mm, "end": v(630, 363.5) * mm});
            skLineSegment(sketch, "E592.trimOffspring", {"start": v(573, 361) * mm, "end": v(630, 361) * mm});
            skLineSegment(sketch, "E593.trimOffspring", {"start": v(573, 324) * mm, "end": v(630, 324) * mm});
            skLineSegment(sketch, "E594.trimOffspring", {"start": v(573, 323) * mm, "end": v(630, 323) * mm});
            skLineSegment(sketch, "E595.trimOffspring", {"start": v(573, 320.5) * mm, "end": v(630, 320.5) * mm});
            skLineSegment(sketch, "E596.trimOffspring", {"start": v(573, 324) * mm, "end": v(573, 363.5) * mm});
            skLineSegment(sketch, "E597.trimOffspring", {"start": v(572, 324) * mm, "end": v(572, 363.5) * mm});
            skLineSegment(sketch, "E598.trimOffspring", {"start": v(515, 363.5) * mm, "end": v(572, 363.5) * mm});
            skLineSegment(sketch, "E599.trimOffspring", {"start": v(515, 361) * mm, "end": v(572, 361) * mm});
            skLineSegment(sketch, "E600.trimOffspring", {"start": v(515, 324) * mm, "end": v(572, 324) * mm});
            skLineSegment(sketch, "E601.trimOffspring", {"start": v(514, 324) * mm, "end": v(514, 363.5) * mm});
            skLineSegment(sketch, "E602.trimOffspring", {"start": v(515, 324) * mm, "end": v(515, 363.5) * mm});
            skLineSegment(sketch, "E603.trimOffspring", {"start": v(515, 323) * mm, "end": v(572, 323) * mm});
            skLineSegment(sketch, "E604.trimOffspring", {"start": v(515, 320.5) * mm, "end": v(572, 320.5) * mm});
            skLineSegment(sketch, "E605.trimOffspring", {"start": v(457, 324) * mm, "end": v(457, 363.5) * mm});
            skLineSegment(sketch, "E606", {"start": v(457, 404) * mm, "end": v(514, 404) * mm});
            skLineSegment(sketch, "E607", {"start": v(457, 401.5) * mm, "end": v(514, 401.5) * mm});
            skLineSegment(sketch, "E608", {"start": v(457, 364.5) * mm, "end": v(514, 364.5) * mm});
            skLineSegment(sketch, "E609.trimOffspring", {"start": v(630, 364.5) * mm, "end": v(630, 404) * mm});
            skLineSegment(sketch, "E610.trimOffspring", {"start": v(573, 404) * mm, "end": v(630, 404) * mm});
            skLineSegment(sketch, "E611.trimOffspring", {"start": v(573, 401.5) * mm, "end": v(630, 401.5) * mm});
            skLineSegment(sketch, "E612.trimOffspring", {"start": v(573, 364.5) * mm, "end": v(630, 364.5) * mm});
            skLineSegment(sketch, "E613.trimOffspring", {"start": v(573, 364.5) * mm, "end": v(573, 404) * mm});
            skLineSegment(sketch, "E614.trimOffspring", {"start": v(572, 364.5) * mm, "end": v(572, 404) * mm});
            skLineSegment(sketch, "E615.trimOffspring", {"start": v(515, 404) * mm, "end": v(572, 404) * mm});
            skLineSegment(sketch, "E616.trimOffspring", {"start": v(515, 401.5) * mm, "end": v(572, 401.5) * mm});
            skLineSegment(sketch, "E617.trimOffspring", {"start": v(515, 364.5) * mm, "end": v(572, 364.5) * mm});
            skLineSegment(sketch, "E618.trimOffspring", {"start": v(514, 364.5) * mm, "end": v(514, 404) * mm});
            skLineSegment(sketch, "E619.trimOffspring", {"start": v(515, 364.5) * mm, "end": v(515, 404) * mm});
            skLineSegment(sketch, "E620.trimOffspring", {"start": v(457, 364.5) * mm, "end": v(457, 404) * mm});
            skLineSegment(sketch, "E621", {"start": v(457, 239.5) * mm, "end": v(514, 239.5) * mm});
            skLineSegment(sketch, "E622.trimOffspring", {"start": v(573, 239.5) * mm, "end": v(630, 239.5) * mm});
            skLineSegment(sketch, "E623.trimOffspring", {"start": v(515, 239.5) * mm, "end": v(572, 239.5) * mm});
            skLineSegment(sketch, "E624", {"start": v(50, 404) * mm, "end": v(50, 405) * mm});
            skLineSegment(sketch, "E625", {"start": v(50, 405) * mm, "end": v(631, 405) * mm});
            skSolve(sketch);
        }
        {
            var Q0;
            Q0=makeQuery(id+"F11.imprint","IMPRINT",FACE,{"disambiguationData":[TD([[makeQuery(id+"F11.imprint","IMPRINT",EDGE,{"derivedFrom":sQuery(id+"F11.wireOp",EDGE,"E72")}),-1.0]])]});
            extrude(context, id + "F12", {"entities" : qUnion([Q0]), "depth" : (getVariable(context, 'DrawerDepth') + getVariable(context, 'Thickness')) * mm});
        }
        {
            var Q0;
            {var subQ0=sQuery(id+"F11.wireOp",EDGE,"E95");Q0=makeQuery(id+"F11.imprint","IMPRINT",FACE,{"disambiguationData":[TD([[makeQuery(id+"F11.imprint","IMPRINT",EDGE,{"derivedFrom":subQ0}),-1.0]])]});}
            var Q1;
            {var subQ0=sQuery(id+"F11.wireOp",EDGE,"E126.trimOffspring");Q1=makeQuery(id+"F11.imprint","IMPRINT",FACE,{"disambiguationData":[TD([[makeQuery(id+"F11.imprint","IMPRINT",EDGE,{"derivedFrom":subQ0}),-1.0]])]});}
            var Q2;
            {var subQ0=sQuery(id+"F11.wireOp",EDGE,"E119.trimOffspring");Q2=makeQuery(id+"F11.imprint","IMPRINT",FACE,{"disambiguationData":[TD([[makeQuery(id+"F11.imprint","IMPRINT",EDGE,{"derivedFrom":subQ0}),-1.0]])]});}
            var Q3;
            {var subQ0=sQuery(id+"F11.wireOp",EDGE,"E122.trimOffspring");Q3=makeQuery(id+"F11.imprint","IMPRINT",FACE,{"disambiguationData":[TD([[makeQuery(id+"F11.imprint","IMPRINT",EDGE,{"derivedFrom":subQ0}),-1.0]])]});}
            var Q4;
            {var subQ0=sQuery(id+"F11.wireOp",EDGE,"E131.trimOffspring");Q4=makeQuery(id+"F11.imprint","IMPRINT",FACE,{"disambiguationData":[TD([[makeQuery(id+"F11.imprint","IMPRINT",EDGE,{"derivedFrom":subQ0}),-1.0]])]});}
            var Q5;
            {var subQ0=sQuery(id+"F11.wireOp",EDGE,"E98");Q5=makeQuery(id+"F11.imprint","IMPRINT",FACE,{"disambiguationData":[TD([[makeQuery(id+"F11.imprint","IMPRINT",EDGE,{"derivedFrom":subQ0}),-1.0]])]});}
            var Q6;
            {var subQ0=sQuery(id+"F11.wireOp",EDGE,"E101");Q6=makeQuery(id+"F11.imprint","IMPRINT",FACE,{"disambiguationData":[TD([[makeQuery(id+"F11.imprint","IMPRINT",EDGE,{"derivedFrom":subQ0}),-1.0]])]});}
            var Q7;
            {var subQ0=sQuery(id+"F11.wireOp",EDGE,"E107.trimOffspring");Q7=makeQuery(id+"F11.imprint","IMPRINT",FACE,{"disambiguationData":[TD([[makeQuery(id+"F11.imprint","IMPRINT",EDGE,{"derivedFrom":subQ0}),-1.0]])]});}
            var Q8;
            {var subQ0=sQuery(id+"F11.wireOp",EDGE,"E114.trimOffspring");Q8=makeQuery(id+"F11.imprint","IMPRINT",FACE,{"disambiguationData":[TD([[makeQuery(id+"F11.imprint","IMPRINT",EDGE,{"derivedFrom":subQ0}),-1.0]])]});}
            var Q9;
            {var subQ0=sQuery(id+"F11.wireOp",EDGE,"E168.trimOffspring");Q9=makeQuery(id+"F11.imprint","IMPRINT",FACE,{"disambiguationData":[TD([[makeQuery(id+"F11.imprint","IMPRINT",EDGE,{"derivedFrom":subQ0}),-1.0]])]});}
            var Q10;
            {var subQ0=sQuery(id+"F11.wireOp",EDGE,"E161.trimOffspring");Q10=makeQuery(id+"F11.imprint","IMPRINT",FACE,{"disambiguationData":[TD([[makeQuery(id+"F11.imprint","IMPRINT",EDGE,{"derivedFrom":subQ0}),-1.0]])]});}
            var Q11;
            {var subQ0=sQuery(id+"F11.wireOp",EDGE,"E155");Q11=makeQuery(id+"F11.imprint","IMPRINT",FACE,{"disambiguationData":[TD([[makeQuery(id+"F11.imprint","IMPRINT",EDGE,{"derivedFrom":subQ0}),-1.0]])]});}
            var Q12;
            {var subQ0=sQuery(id+"F11.wireOp",EDGE,"E152");Q12=makeQuery(id+"F11.imprint","IMPRINT",FACE,{"disambiguationData":[TD([[makeQuery(id+"F11.imprint","IMPRINT",EDGE,{"derivedFrom":subQ0}),-1.0]])]});}
            var Q13;
            {var subQ0=sQuery(id+"F11.wireOp",EDGE,"E185.trimOffspring");Q13=makeQuery(id+"F11.imprint","IMPRINT",FACE,{"disambiguationData":[TD([[makeQuery(id+"F11.imprint","IMPRINT",EDGE,{"derivedFrom":subQ0}),-1.0]])]});}
            var Q14;
            {var subQ0=sQuery(id+"F11.wireOp",EDGE,"E176.trimOffspring");Q14=makeQuery(id+"F11.imprint","IMPRINT",FACE,{"disambiguationData":[TD([[makeQuery(id+"F11.imprint","IMPRINT",EDGE,{"derivedFrom":subQ0}),-1.0]])]});}
            var Q15;
            {var subQ0=sQuery(id+"F11.wireOp",EDGE,"E173.trimOffspring");Q15=makeQuery(id+"F11.imprint","IMPRINT",FACE,{"disambiguationData":[TD([[makeQuery(id+"F11.imprint","IMPRINT",EDGE,{"derivedFrom":subQ0}),-1.0]])]});}
            var Q16;
            {var subQ0=sQuery(id+"F11.wireOp",EDGE,"E180.trimOffspring");Q16=makeQuery(id+"F11.imprint","IMPRINT",FACE,{"disambiguationData":[TD([[makeQuery(id+"F11.imprint","IMPRINT",EDGE,{"derivedFrom":subQ0}),-1.0]])]});}
            var Q17;
            {var subQ0=sQuery(id+"F11.wireOp",EDGE,"E149");Q17=makeQuery(id+"F11.imprint","IMPRINT",FACE,{"disambiguationData":[TD([[makeQuery(id+"F11.imprint","IMPRINT",EDGE,{"derivedFrom":subQ0}),-1.0]])]});}
            var Q18;
            {var subQ0=sQuery(id+"F11.wireOp",EDGE,"E208");Q18=makeQuery(id+"F11.imprint","IMPRINT",FACE,{"disambiguationData":[TD([[makeQuery(id+"F11.imprint","IMPRINT",EDGE,{"derivedFrom":subQ0}),-1.0]])]});}
            var Q19;
            {var subQ0=sQuery(id+"F11.wireOp",EDGE,"E214.trimOffspring");Q19=makeQuery(id+"F11.imprint","IMPRINT",FACE,{"disambiguationData":[TD([[makeQuery(id+"F11.imprint","IMPRINT",EDGE,{"derivedFrom":subQ0}),-1.0]])]});}
            var Q20;
            {var subQ0=sQuery(id+"F11.wireOp",EDGE,"E221.trimOffspring");Q20=makeQuery(id+"F11.imprint","IMPRINT",FACE,{"disambiguationData":[TD([[makeQuery(id+"F11.imprint","IMPRINT",EDGE,{"derivedFrom":subQ0}),-1.0]])]});}
            var Q21;
            {var subQ0=sQuery(id+"F11.wireOp",EDGE,"E229.trimOffspring");Q21=makeQuery(id+"F11.imprint","IMPRINT",FACE,{"disambiguationData":[TD([[makeQuery(id+"F11.imprint","IMPRINT",EDGE,{"derivedFrom":subQ0}),-1.0]])]});}
            var Q22;
            {var subQ0=sQuery(id+"F11.wireOp",EDGE,"E238.trimOffspring");Q22=makeQuery(id+"F11.imprint","IMPRINT",FACE,{"disambiguationData":[TD([[makeQuery(id+"F11.imprint","IMPRINT",EDGE,{"derivedFrom":subQ0}),-1.0]])]});}
            var Q23;
            {var subQ0=sQuery(id+"F11.wireOp",EDGE,"E205");Q23=makeQuery(id+"F11.imprint","IMPRINT",FACE,{"disambiguationData":[TD([[makeQuery(id+"F11.imprint","IMPRINT",EDGE,{"derivedFrom":subQ0}),-1.0]])]});}
            var Q24;
            {var subQ0=sQuery(id+"F11.wireOp",EDGE,"E202");Q24=makeQuery(id+"F11.imprint","IMPRINT",FACE,{"disambiguationData":[TD([[makeQuery(id+"F11.imprint","IMPRINT",EDGE,{"derivedFrom":subQ0}),-1.0]])]});}
            var Q25;
            {var subQ0=sQuery(id+"F11.wireOp",EDGE,"E233.trimOffspring");Q25=makeQuery(id+"F11.imprint","IMPRINT",FACE,{"disambiguationData":[TD([[makeQuery(id+"F11.imprint","IMPRINT",EDGE,{"derivedFrom":subQ0}),-1.0]])]});}
            var Q26;
            {var subQ0=sQuery(id+"F11.wireOp",EDGE,"E226.trimOffspring");Q26=makeQuery(id+"F11.imprint","IMPRINT",FACE,{"disambiguationData":[TD([[makeQuery(id+"F11.imprint","IMPRINT",EDGE,{"derivedFrom":subQ0}),-1.0]])]});}
            var Q27;
            {var subQ0=sQuery(id+"F11.wireOp",EDGE,"E358");Q27=makeQuery(id+"F11.imprint","IMPRINT",FACE,{"disambiguationData":[TD([[makeQuery(id+"F11.imprint","IMPRINT",EDGE,{"derivedFrom":subQ0}),-1.0]])]});}
            var Q28;
            {var subQ0=sQuery(id+"F11.wireOp",EDGE,"E389.trimOffspring");Q28=makeQuery(id+"F11.imprint","IMPRINT",FACE,{"disambiguationData":[TD([[makeQuery(id+"F11.imprint","IMPRINT",EDGE,{"derivedFrom":subQ0}),-1.0]])]});}
            var Q29;
            {var subQ0=sQuery(id+"F11.wireOp",EDGE,"E382.trimOffspring");Q29=makeQuery(id+"F11.imprint","IMPRINT",FACE,{"disambiguationData":[TD([[makeQuery(id+"F11.imprint","IMPRINT",EDGE,{"derivedFrom":subQ0}),-1.0]])]});}
            var Q30;
            {var subQ0=sQuery(id+"F11.wireOp",EDGE,"E456.trimOffspring");Q30=makeQuery(id+"F11.imprint","IMPRINT",FACE,{"disambiguationData":[TD([[makeQuery(id+"F11.imprint","IMPRINT",EDGE,{"derivedFrom":subQ0}),-1.0]])]});}
            var Q31;
            {var subQ0=sQuery(id+"F11.wireOp",EDGE,"E459.trimOffspring");Q31=makeQuery(id+"F11.imprint","IMPRINT",FACE,{"disambiguationData":[TD([[makeQuery(id+"F11.imprint","IMPRINT",EDGE,{"derivedFrom":subQ0}),-1.0]])]});}
            var Q32;
            {var subQ0=sQuery(id+"F11.wireOp",EDGE,"E385.trimOffspring");Q32=makeQuery(id+"F11.imprint","IMPRINT",FACE,{"disambiguationData":[TD([[makeQuery(id+"F11.imprint","IMPRINT",EDGE,{"derivedFrom":subQ0}),-1.0]])]});}
            var Q33;
            {var subQ0=sQuery(id+"F11.wireOp",EDGE,"E394.trimOffspring");Q33=makeQuery(id+"F11.imprint","IMPRINT",FACE,{"disambiguationData":[TD([[makeQuery(id+"F11.imprint","IMPRINT",EDGE,{"derivedFrom":subQ0}),-1.0]])]});}
            var Q34;
            {var subQ0=sQuery(id+"F11.wireOp",EDGE,"E361");Q34=makeQuery(id+"F11.imprint","IMPRINT",FACE,{"disambiguationData":[TD([[makeQuery(id+"F11.imprint","IMPRINT",EDGE,{"derivedFrom":subQ0}),-1.0]])]});}
            var Q35;
            {var subQ0=sQuery(id+"F11.wireOp",EDGE,"E364");Q35=makeQuery(id+"F11.imprint","IMPRINT",FACE,{"disambiguationData":[TD([[makeQuery(id+"F11.imprint","IMPRINT",EDGE,{"derivedFrom":subQ0}),-1.0]])]});}
            var Q36;
            {var subQ0=sQuery(id+"F11.wireOp",EDGE,"E370.trimOffspring");Q36=makeQuery(id+"F11.imprint","IMPRINT",FACE,{"disambiguationData":[TD([[makeQuery(id+"F11.imprint","IMPRINT",EDGE,{"derivedFrom":subQ0}),-1.0]])]});}
            var Q37;
            {var subQ0=sQuery(id+"F11.wireOp",EDGE,"E377.trimOffspring");Q37=makeQuery(id+"F11.imprint","IMPRINT",FACE,{"disambiguationData":[TD([[makeQuery(id+"F11.imprint","IMPRINT",EDGE,{"derivedFrom":subQ0}),-1.0]])]});}
            var Q38;
            {var subQ0=sQuery(id+"F11.wireOp",EDGE,"E451.trimOffspring");Q38=makeQuery(id+"F11.imprint","IMPRINT",FACE,{"disambiguationData":[TD([[makeQuery(id+"F11.imprint","IMPRINT",EDGE,{"derivedFrom":subQ0}),-1.0]])]});}
            var Q39;
            {var subQ0=sQuery(id+"F11.wireOp",EDGE,"E441.trimOffspring");Q39=makeQuery(id+"F11.imprint","IMPRINT",FACE,{"disambiguationData":[TD([[makeQuery(id+"F11.imprint","IMPRINT",EDGE,{"derivedFrom":subQ0}),-1.0]])]});}
            var Q40;
            {var subQ0=sQuery(id+"F11.wireOp",EDGE,"E339.trimOffspring");Q40=makeQuery(id+"F11.imprint","IMPRINT",FACE,{"disambiguationData":[TD([[makeQuery(id+"F11.imprint","IMPRINT",EDGE,{"derivedFrom":subQ0}),-1.0]])]});}
            var Q41;
            {var subQ0=sQuery(id+"F11.wireOp",EDGE,"E345.trimOffspring");Q41=makeQuery(id+"F11.imprint","IMPRINT",FACE,{"disambiguationData":[TD([[makeQuery(id+"F11.imprint","IMPRINT",EDGE,{"derivedFrom":subQ0}),-1.0]])]});}
            var Q42;
            {var subQ0=sQuery(id+"F11.wireOp",EDGE,"E316");Q42=makeQuery(id+"F11.imprint","IMPRINT",FACE,{"disambiguationData":[TD([[makeQuery(id+"F11.imprint","IMPRINT",EDGE,{"derivedFrom":subQ0}),-1.0]])]});}
            var Q43;
            {var subQ0=sQuery(id+"F11.wireOp",EDGE,"E318");Q43=makeQuery(id+"F11.imprint","IMPRINT",FACE,{"disambiguationData":[TD([[makeQuery(id+"F11.imprint","IMPRINT",EDGE,{"derivedFrom":subQ0}),-1.0]])]});}
            var Q44;
            {var subQ0=sQuery(id+"F11.wireOp",EDGE,"E349.trimOffspring");Q44=makeQuery(id+"F11.imprint","IMPRINT",FACE,{"disambiguationData":[TD([[makeQuery(id+"F11.imprint","IMPRINT",EDGE,{"derivedFrom":subQ0}),-1.0]])]});}
            var Q45;
            {var subQ0=sQuery(id+"F11.wireOp",EDGE,"E341.trimOffspring");Q45=makeQuery(id+"F11.imprint","IMPRINT",FACE,{"disambiguationData":[TD([[makeQuery(id+"F11.imprint","IMPRINT",EDGE,{"derivedFrom":subQ0}),-1.0]])]});}
            var Q46;
            {var subQ0=sQuery(id+"F11.wireOp",EDGE,"E444.trimOffspring");Q46=makeQuery(id+"F11.imprint","IMPRINT",FACE,{"disambiguationData":[TD([[makeQuery(id+"F11.imprint","IMPRINT",EDGE,{"derivedFrom":subQ0}),-1.0]])]});}
            var Q47;
            {var subQ0=sQuery(id+"F11.wireOp",EDGE,"E436.trimOffspring");Q47=makeQuery(id+"F11.imprint","IMPRINT",FACE,{"disambiguationData":[TD([[makeQuery(id+"F11.imprint","IMPRINT",EDGE,{"derivedFrom":subQ0}),-1.0]])]});}
            var Q48;
            {var subQ0=sQuery(id+"F11.wireOp",EDGE,"E334.trimOffspring");Q48=makeQuery(id+"F11.imprint","IMPRINT",FACE,{"disambiguationData":[TD([[makeQuery(id+"F11.imprint","IMPRINT",EDGE,{"derivedFrom":subQ0}),-1.0]])]});}
            var Q49;
            {var subQ0=sQuery(id+"F11.wireOp",EDGE,"E327.trimOffspring");Q49=makeQuery(id+"F11.imprint","IMPRINT",FACE,{"disambiguationData":[TD([[makeQuery(id+"F11.imprint","IMPRINT",EDGE,{"derivedFrom":subQ0}),-1.0]])]});}
            var Q50;
            {var subQ0=sQuery(id+"F11.wireOp",EDGE,"E321");Q50=makeQuery(id+"F11.imprint","IMPRINT",FACE,{"disambiguationData":[TD([[makeQuery(id+"F11.imprint","IMPRINT",EDGE,{"derivedFrom":subQ0}),-1.0]])]});}
            var Q51;
            {var subQ0=sQuery(id+"F11.wireOp",EDGE,"E271");Q51=makeQuery(id+"F11.imprint","IMPRINT",FACE,{"disambiguationData":[TD([[makeQuery(id+"F11.imprint","IMPRINT",EDGE,{"derivedFrom":subQ0}),-1.0]])]});}
            var Q52;
            {var subQ0=sQuery(id+"F11.wireOp",EDGE,"E302.trimOffspring");Q52=makeQuery(id+"F11.imprint","IMPRINT",FACE,{"disambiguationData":[TD([[makeQuery(id+"F11.imprint","IMPRINT",EDGE,{"derivedFrom":subQ0}),-1.0]])]});}
            var Q53;
            {var subQ0=sQuery(id+"F11.wireOp",EDGE,"E295.trimOffspring");Q53=makeQuery(id+"F11.imprint","IMPRINT",FACE,{"disambiguationData":[TD([[makeQuery(id+"F11.imprint","IMPRINT",EDGE,{"derivedFrom":subQ0}),-1.0]])]});}
            var Q54;
            {var subQ0=sQuery(id+"F11.wireOp",EDGE,"E426.trimOffspring");Q54=makeQuery(id+"F11.imprint","IMPRINT",FACE,{"disambiguationData":[TD([[makeQuery(id+"F11.imprint","IMPRINT",EDGE,{"derivedFrom":subQ0}),-1.0]])]});}
            var Q55;
            {var subQ0=sQuery(id+"F11.wireOp",EDGE,"E429.trimOffspring");Q55=makeQuery(id+"F11.imprint","IMPRINT",FACE,{"disambiguationData":[TD([[makeQuery(id+"F11.imprint","IMPRINT",EDGE,{"derivedFrom":subQ0}),-1.0]])]});}
            var Q56;
            {var subQ0=sQuery(id+"F11.wireOp",EDGE,"E298.trimOffspring");Q56=makeQuery(id+"F11.imprint","IMPRINT",FACE,{"disambiguationData":[TD([[makeQuery(id+"F11.imprint","IMPRINT",EDGE,{"derivedFrom":subQ0}),-1.0]])]});}
            var Q57;
            {var subQ0=sQuery(id+"F11.wireOp",EDGE,"E307.trimOffspring");Q57=makeQuery(id+"F11.imprint","IMPRINT",FACE,{"disambiguationData":[TD([[makeQuery(id+"F11.imprint","IMPRINT",EDGE,{"derivedFrom":subQ0}),-1.0]])]});}
            var Q58;
            {var subQ0=sQuery(id+"F11.wireOp",EDGE,"E274");Q58=makeQuery(id+"F11.imprint","IMPRINT",FACE,{"disambiguationData":[TD([[makeQuery(id+"F11.imprint","IMPRINT",EDGE,{"derivedFrom":subQ0}),-1.0]])]});}
            var Q59;
            {var subQ0=sQuery(id+"F11.wireOp",EDGE,"E277");Q59=makeQuery(id+"F11.imprint","IMPRINT",FACE,{"disambiguationData":[TD([[makeQuery(id+"F11.imprint","IMPRINT",EDGE,{"derivedFrom":subQ0}),-1.0]])]});}
            var Q60;
            {var subQ0=sQuery(id+"F11.wireOp",EDGE,"E283.trimOffspring");Q60=makeQuery(id+"F11.imprint","IMPRINT",FACE,{"disambiguationData":[TD([[makeQuery(id+"F11.imprint","IMPRINT",EDGE,{"derivedFrom":subQ0}),-1.0]])]});}
            var Q61;
            {var subQ0=sQuery(id+"F11.wireOp",EDGE,"E290.trimOffspring");Q61=makeQuery(id+"F11.imprint","IMPRINT",FACE,{"disambiguationData":[TD([[makeQuery(id+"F11.imprint","IMPRINT",EDGE,{"derivedFrom":subQ0}),-1.0]])]});}
            var Q62;
            {var subQ0=sQuery(id+"F11.wireOp",EDGE,"E421.trimOffspring");Q62=makeQuery(id+"F11.imprint","IMPRINT",FACE,{"disambiguationData":[TD([[makeQuery(id+"F11.imprint","IMPRINT",EDGE,{"derivedFrom":subQ0}),-1.0]])]});}
            var Q63;
            {var subQ0=sQuery(id+"F11.wireOp",EDGE,"E244");Q63=makeQuery(id+"F11.imprint","IMPRINT",FACE,{"disambiguationData":[TD([[makeQuery(id+"F11.imprint","IMPRINT",EDGE,{"derivedFrom":subQ0}),-1.0]])]});}
            var Q64;
            {var subQ0=sQuery(id+"F11.wireOp",EDGE,"E253.trimOffspring");Q64=makeQuery(id+"F11.imprint","IMPRINT",FACE,{"disambiguationData":[TD([[makeQuery(id+"F11.imprint","IMPRINT",EDGE,{"derivedFrom":subQ0}),-1.0]])]});}
            var Q65;
            {var subQ0=sQuery(id+"F11.wireOp",EDGE,"E248.trimOffspring");Q65=makeQuery(id+"F11.imprint","IMPRINT",FACE,{"disambiguationData":[TD([[makeQuery(id+"F11.imprint","IMPRINT",EDGE,{"derivedFrom":subQ0}),-1.0]])]});}
            var Q66;
            {var subQ0=sQuery(id+"F11.wireOp",EDGE,"E397");Q66=makeQuery(id+"F11.imprint","IMPRINT",FACE,{"disambiguationData":[TD([[makeQuery(id+"F11.imprint","IMPRINT",EDGE,{"derivedFrom":subQ0}),-1.0]])]});}
            var Q67;
            {var subQ0=sQuery(id+"F11.wireOp",EDGE,"E406.trimOffspring");Q67=makeQuery(id+"F11.imprint","IMPRINT",FACE,{"disambiguationData":[TD([[makeQuery(id+"F11.imprint","IMPRINT",EDGE,{"derivedFrom":subQ0}),-1.0]])]});}
            var Q68;
            {var subQ0=sQuery(id+"F11.wireOp",EDGE,"E401.trimOffspring");Q68=makeQuery(id+"F11.imprint","IMPRINT",FACE,{"disambiguationData":[TD([[makeQuery(id+"F11.imprint","IMPRINT",EDGE,{"derivedFrom":subQ0}),-1.0]])]});}
            var Q69;
            {var subQ0=sQuery(id+"F11.wireOp",EDGE,"E463.trimOffspring");Q69=makeQuery(id+"F11.imprint","IMPRINT",FACE,{"disambiguationData":[TD([[makeQuery(id+"F11.imprint","IMPRINT",EDGE,{"derivedFrom":subQ0}),-1.0]])]});}
            var Q70;
            {var subQ0=sQuery(id+"F11.wireOp",EDGE,"E606");Q70=makeQuery(id+"F11.imprint","IMPRINT",FACE,{"disambiguationData":[TD([[makeQuery(id+"F11.imprint","IMPRINT",EDGE,{"derivedFrom":subQ0}),-1.0]])]});}
            var Q71;
            {var subQ0=sQuery(id+"F11.wireOp",EDGE,"E567");Q71=makeQuery(id+"F11.imprint","IMPRINT",FACE,{"disambiguationData":[TD([[makeQuery(id+"F11.imprint","IMPRINT",EDGE,{"derivedFrom":subQ0}),-1.0]])]});}
            var Q72;
            {var subQ0=sQuery(id+"F11.wireOp",EDGE,"E570");Q72=makeQuery(id+"F11.imprint","IMPRINT",FACE,{"disambiguationData":[TD([[makeQuery(id+"F11.imprint","IMPRINT",EDGE,{"derivedFrom":subQ0}),-1.0]])]});}
            var Q73;
            {var subQ0=sQuery(id+"F11.wireOp",EDGE,"E573");Q73=makeQuery(id+"F11.imprint","IMPRINT",FACE,{"disambiguationData":[TD([[makeQuery(id+"F11.imprint","IMPRINT",EDGE,{"derivedFrom":subQ0}),-1.0]])]});}
            var Q74;
            {var subQ0=sQuery(id+"F11.wireOp",EDGE,"E525");Q74=makeQuery(id+"F11.imprint","IMPRINT",FACE,{"disambiguationData":[TD([[makeQuery(id+"F11.imprint","IMPRINT",EDGE,{"derivedFrom":subQ0}),-1.0]])]});}
            var Q75;
            {var subQ0=sQuery(id+"F11.wireOp",EDGE,"E527");Q75=makeQuery(id+"F11.imprint","IMPRINT",FACE,{"disambiguationData":[TD([[makeQuery(id+"F11.imprint","IMPRINT",EDGE,{"derivedFrom":subQ0}),-1.0]])]});}
            var Q76;
            {var subQ0=sQuery(id+"F11.wireOp",EDGE,"E530");Q76=makeQuery(id+"F11.imprint","IMPRINT",FACE,{"disambiguationData":[TD([[makeQuery(id+"F11.imprint","IMPRINT",EDGE,{"derivedFrom":subQ0}),-1.0]])]});}
            var Q77;
            {var subQ0=sQuery(id+"F11.wireOp",EDGE,"E480");Q77=makeQuery(id+"F11.imprint","IMPRINT",FACE,{"disambiguationData":[TD([[makeQuery(id+"F11.imprint","IMPRINT",EDGE,{"derivedFrom":subQ0}),-1.0]])]});}
            var Q78;
            {var subQ0=sQuery(id+"F11.wireOp",EDGE,"E483");Q78=makeQuery(id+"F11.imprint","IMPRINT",FACE,{"disambiguationData":[TD([[makeQuery(id+"F11.imprint","IMPRINT",EDGE,{"derivedFrom":subQ0}),-1.0]])]});}
            var Q79;
            {var subQ0=sQuery(id+"F11.wireOp",EDGE,"E486");Q79=makeQuery(id+"F11.imprint","IMPRINT",FACE,{"disambiguationData":[TD([[makeQuery(id+"F11.imprint","IMPRINT",EDGE,{"derivedFrom":subQ0}),-1.0]])]});}
            var Q80;
            {var subQ0=sQuery(id+"F11.wireOp",EDGE,"E615.trimOffspring");Q80=makeQuery(id+"F11.imprint","IMPRINT",FACE,{"disambiguationData":[TD([[makeQuery(id+"F11.imprint","IMPRINT",EDGE,{"derivedFrom":subQ0}),-1.0]])]});}
            var Q81;
            {var subQ0=sQuery(id+"F11.wireOp",EDGE,"E610.trimOffspring");Q81=makeQuery(id+"F11.imprint","IMPRINT",FACE,{"disambiguationData":[TD([[makeQuery(id+"F11.imprint","IMPRINT",EDGE,{"derivedFrom":subQ0}),-1.0]])]});}
            var Q82;
            {var subQ0=sQuery(id+"F11.wireOp",EDGE,"E598.trimOffspring");Q82=makeQuery(id+"F11.imprint","IMPRINT",FACE,{"disambiguationData":[TD([[makeQuery(id+"F11.imprint","IMPRINT",EDGE,{"derivedFrom":subQ0}),-1.0]])]});}
            var Q83;
            {var subQ0=sQuery(id+"F11.wireOp",EDGE,"E591.trimOffspring");Q83=makeQuery(id+"F11.imprint","IMPRINT",FACE,{"disambiguationData":[TD([[makeQuery(id+"F11.imprint","IMPRINT",EDGE,{"derivedFrom":subQ0}),-1.0]])]});}
            var Q84;
            {var subQ0=sQuery(id+"F11.wireOp",EDGE,"E603.trimOffspring");Q84=makeQuery(id+"F11.imprint","IMPRINT",FACE,{"disambiguationData":[TD([[makeQuery(id+"F11.imprint","IMPRINT",EDGE,{"derivedFrom":subQ0}),-1.0]])]});}
            var Q85;
            {var subQ0=sQuery(id+"F11.wireOp",EDGE,"E594.trimOffspring");Q85=makeQuery(id+"F11.imprint","IMPRINT",FACE,{"disambiguationData":[TD([[makeQuery(id+"F11.imprint","IMPRINT",EDGE,{"derivedFrom":subQ0}),-1.0]])]});}
            var Q86;
            {var subQ0=sQuery(id+"F11.wireOp",EDGE,"E586.trimOffspring");Q86=makeQuery(id+"F11.imprint","IMPRINT",FACE,{"disambiguationData":[TD([[makeQuery(id+"F11.imprint","IMPRINT",EDGE,{"derivedFrom":subQ0}),-1.0]])]});}
            var Q87;
            {var subQ0=sQuery(id+"F11.wireOp",EDGE,"E554.trimOffspring");Q87=makeQuery(id+"F11.imprint","IMPRINT",FACE,{"disambiguationData":[TD([[makeQuery(id+"F11.imprint","IMPRINT",EDGE,{"derivedFrom":subQ0}),-1.0]])]});}
            var Q88;
            {var subQ0=sQuery(id+"F11.wireOp",EDGE,"E548.trimOffspring");Q88=makeQuery(id+"F11.imprint","IMPRINT",FACE,{"disambiguationData":[TD([[makeQuery(id+"F11.imprint","IMPRINT",EDGE,{"derivedFrom":subQ0}),-1.0]])]});}
            var Q89;
            {var subQ0=sQuery(id+"F11.wireOp",EDGE,"E558.trimOffspring");Q89=makeQuery(id+"F11.imprint","IMPRINT",FACE,{"disambiguationData":[TD([[makeQuery(id+"F11.imprint","IMPRINT",EDGE,{"derivedFrom":subQ0}),-1.0]])]});}
            var Q90;
            {var subQ0=sQuery(id+"F11.wireOp",EDGE,"E550.trimOffspring");Q90=makeQuery(id+"F11.imprint","IMPRINT",FACE,{"disambiguationData":[TD([[makeQuery(id+"F11.imprint","IMPRINT",EDGE,{"derivedFrom":subQ0}),-1.0]])]});}
            var Q91;
            {var subQ0=sQuery(id+"F11.wireOp",EDGE,"E536.trimOffspring");Q91=makeQuery(id+"F11.imprint","IMPRINT",FACE,{"disambiguationData":[TD([[makeQuery(id+"F11.imprint","IMPRINT",EDGE,{"derivedFrom":subQ0}),-1.0]])]});}
            var Q92;
            {var subQ0=sQuery(id+"F11.wireOp",EDGE,"E543.trimOffspring");Q92=makeQuery(id+"F11.imprint","IMPRINT",FACE,{"disambiguationData":[TD([[makeQuery(id+"F11.imprint","IMPRINT",EDGE,{"derivedFrom":subQ0}),-1.0]])]});}
            var Q93;
            {var subQ0=sQuery(id+"F11.wireOp",EDGE,"E511.trimOffspring");Q93=makeQuery(id+"F11.imprint","IMPRINT",FACE,{"disambiguationData":[TD([[makeQuery(id+"F11.imprint","IMPRINT",EDGE,{"derivedFrom":subQ0}),-1.0]])]});}
            var Q94;
            {var subQ0=sQuery(id+"F11.wireOp",EDGE,"E504.trimOffspring");Q94=makeQuery(id+"F11.imprint","IMPRINT",FACE,{"disambiguationData":[TD([[makeQuery(id+"F11.imprint","IMPRINT",EDGE,{"derivedFrom":subQ0}),-1.0]])]});}
            var Q95;
            {var subQ0=sQuery(id+"F11.wireOp",EDGE,"E516.trimOffspring");Q95=makeQuery(id+"F11.imprint","IMPRINT",FACE,{"disambiguationData":[TD([[makeQuery(id+"F11.imprint","IMPRINT",EDGE,{"derivedFrom":subQ0}),-1.0]])]});}
            var Q96;
            {var subQ0=sQuery(id+"F11.wireOp",EDGE,"E507.trimOffspring");Q96=makeQuery(id+"F11.imprint","IMPRINT",FACE,{"disambiguationData":[TD([[makeQuery(id+"F11.imprint","IMPRINT",EDGE,{"derivedFrom":subQ0}),-1.0]])]});}
            var Q97;
            {var subQ0=sQuery(id+"F11.wireOp",EDGE,"E492.trimOffspring");Q97=makeQuery(id+"F11.imprint","IMPRINT",FACE,{"disambiguationData":[TD([[makeQuery(id+"F11.imprint","IMPRINT",EDGE,{"derivedFrom":subQ0}),-1.0]])]});}
            var Q98;
            {var subQ0=sQuery(id+"F11.wireOp",EDGE,"E499.trimOffspring");Q98=makeQuery(id+"F11.imprint","IMPRINT",FACE,{"disambiguationData":[TD([[makeQuery(id+"F11.imprint","IMPRINT",EDGE,{"derivedFrom":subQ0}),-1.0]])]});}
            var Q99;
            {var subQ0=sQuery(id+"F11.wireOp",EDGE,"E579.trimOffspring");Q99=makeQuery(id+"F11.imprint","IMPRINT",FACE,{"disambiguationData":[TD([[makeQuery(id+"F11.imprint","IMPRINT",EDGE,{"derivedFrom":subQ0}),-1.0]])]});}
            extrude(context, id + "F13", {"entities" : qUnion([Q0, Q1, Q2, Q3, Q4, Q5, Q6, Q7, Q8, Q9, Q10, Q11, Q12, Q13, Q14, Q15, Q16, Q17, Q18, Q19, Q20, Q21, Q22, Q23, Q24, Q25, Q26, Q27, Q28, Q29, Q30, Q31, Q32, Q33, Q34, Q35, Q36, Q37, Q38, Q39, Q40, Q41, Q42, Q43, Q44, Q45, Q46, Q47, Q48, Q49, Q50, Q51, Q52, Q53, Q54, Q55, Q56, Q57, Q58, Q59, Q60, Q61, Q62, Q63, Q64, Q65, Q66, Q67, Q68, Q69, Q70, Q71, Q72, Q73, Q74, Q75, Q76, Q77, Q78, Q79, Q80, Q81, Q82, Q83, Q84, Q85, Q86, Q87, Q88, Q89, Q90, Q91, Q92, Q93, Q94, Q95, Q96, Q97, Q98, Q99]), "operationType" : NewBodyOperationType.ADD, "depth" : (getVariable(context, 'Thickness')) * mm});
        }
        {
            var Q0;
            Q0=qCreatedBy(makeId("Right.planeOp"),FACE);
            var sketch = newSketch(context, id + "F14", { "sketchPlane" : qUnion([Q0])});
            skLineSegment(sketch, "E626.bottom", {"start": v(50, -1) * mm, "end": v(225, -1) * mm, "construction": true});
            skLineSegment(sketch, "E626.top", {"start": v(50, 121.5) * mm, "end": v(225, 121.5) * mm});
            skLineSegment(sketch, "E626.left", {"start": v(50, -1) * mm, "end": v(50, 121.5) * mm, "construction": true});
            skLineSegment(sketch, "E626.right", {"start": v(225, -1) * mm, "end": v(225, 121.5) * mm});
            skLineSegment(sketch, "E627", {"start": v(50, 121.5) * mm, "end": v(50, 405) * mm});
            skLineSegment(sketch, "E628", {"start": v(50, 405) * mm, "end": v(631, 405) * mm});
            skLineSegment(sketch, "E629", {"start": v(631, 405) * mm, "end": v(631, -1) * mm});
            skLineSegment(sketch, "E630", {"start": v(631, -1) * mm, "end": v(225, -1) * mm});
            skSolve(sketch);
        }
        {
            var Q0;
            Q0=qSketchRegion(id+"F14",true);
            extrude(context, id + "F15", {"entities" : qUnion([Q0]), "operationType" : NewBodyOperationType.REMOVE, "endBound" : BoundingType.THROUGH_ALL, "depth" : 25 * mm});
        }
    });
